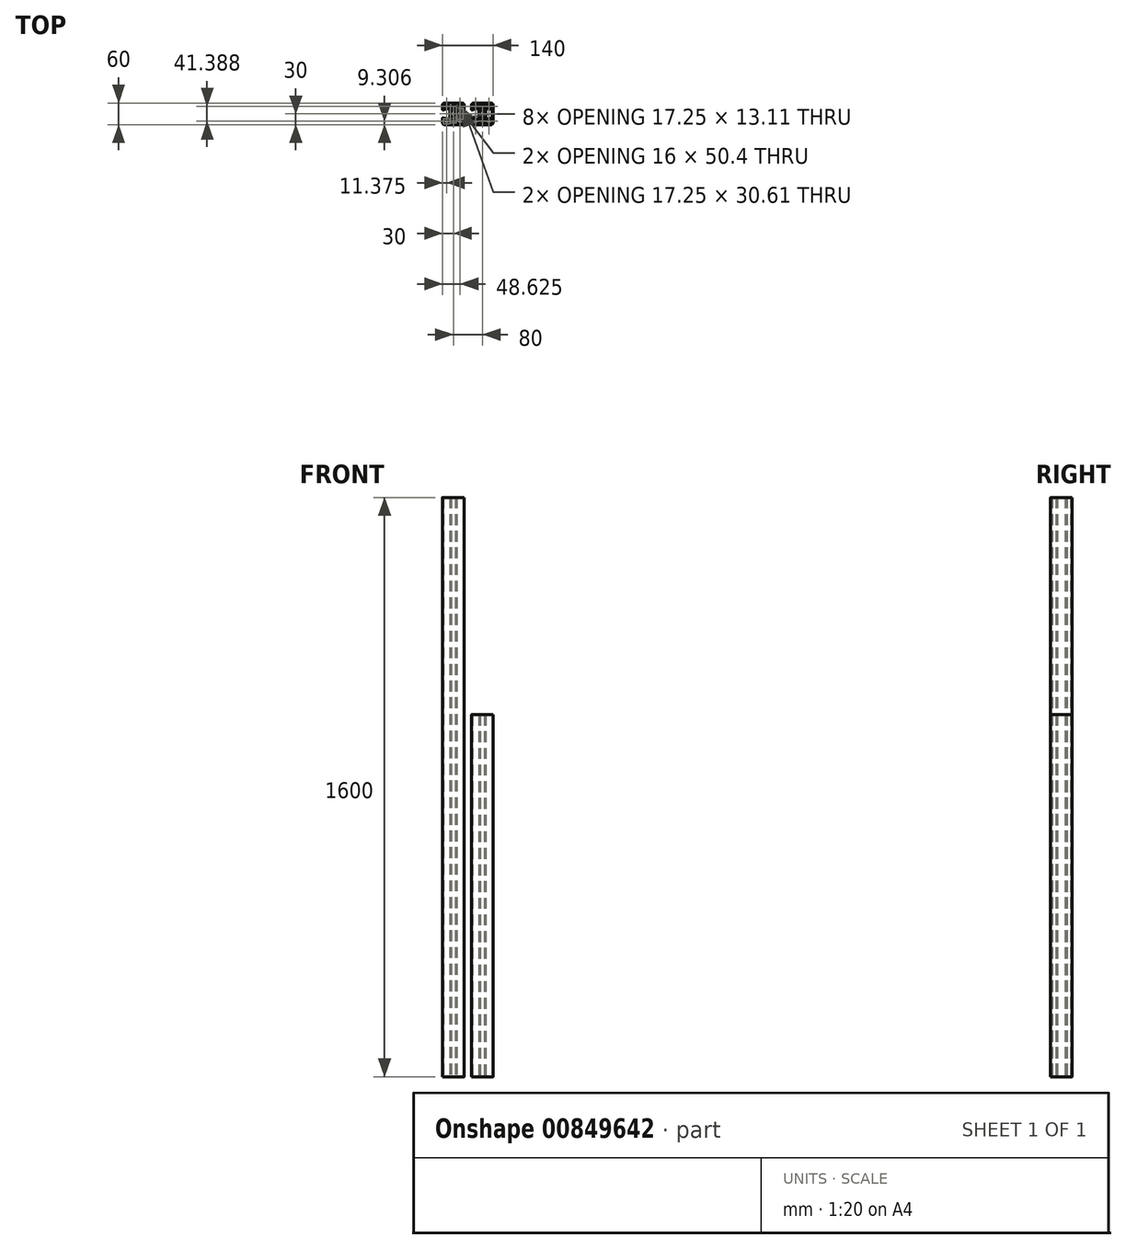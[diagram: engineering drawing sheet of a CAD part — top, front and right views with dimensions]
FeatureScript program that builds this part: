
annotation { "Feature Type Name" : "Feature", "Feature Type Description" : "" }
export const myFeature = defineFeature(function(context is Context, id is Id, definition is map)
    precondition{}
    {
        {
            var Q0;
            Q0=qCreatedBy(makeId("Top.planeOp"),FACE);
            var sketch = newSketch(context, id + "F0", { "sketchPlane" : qUnion([Q0])});
            skLineSegment(sketch, "E0", {"start": v(11.26, -15.27) * mm, "end": v(26.88, -11.09) * mm});
            skLineSegment(sketch, "E1", {"start": v(27.25, -10.6) * mm, "end": v(27.25, 10.6) * mm});
            skLineSegment(sketch, "E2", {"start": v(26.88, 11.09) * mm, "end": v(11.26, 15.27) * mm});
            skLineSegment(sketch, "E3", {"start": v(10, 14.3) * mm, "end": v(10, -14.3) * mm});
            skLineSegment(sketch, "E4", {"start": v(24, 27.25) * mm, "end": v(11, 27.25) * mm});
            skLineSegment(sketch, "E5", {"start": v(10, 26.25) * mm, "end": v(10, 19.22) * mm});
            skLineSegment(sketch, "E6", {"start": v(10.74, 18.26) * mm, "end": v(26, 14.17) * mm});
            skLineSegment(sketch, "E7", {"start": v(27.25, 15.14) * mm, "end": v(27.25, 24) * mm});
            skLineSegment(sketch, "E8", {"start": v(26, -14.17) * mm, "end": v(10.74, -18.26) * mm});
            skLineSegment(sketch, "E9", {"start": v(10, -19.22) * mm, "end": v(10, -26.25) * mm});
            skLineSegment(sketch, "E10", {"start": v(11, -27.25) * mm, "end": v(24, -27.25) * mm});
            skLineSegment(sketch, "E11", {"start": v(27.25, -24) * mm, "end": v(27.25, -15.14) * mm});
            skLineSegment(sketch, "E12", {"start": v(-10, 14.3) * mm, "end": v(-10, -14.3) * mm});
            skLineSegment(sketch, "E13", {"start": v(-28.43, 10.67) * mm, "end": v(-11.26, 15.27) * mm});
            skLineSegment(sketch, "E14", {"start": v(-30, 24) * mm, "end": v(-30, 11.88) * mm});
            skLineSegment(sketch, "E15", {"start": v(24, 30) * mm, "end": v(-24, 30) * mm});
            skLineSegment(sketch, "E16", {"start": v(30, -24) * mm, "end": v(30, 24) * mm});
            skLineSegment(sketch, "E17", {"start": v(-24, -30) * mm, "end": v(24, -30) * mm});
            skLineSegment(sketch, "E18", {"start": v(-30, -11.88) * mm, "end": v(-30, -24) * mm});
            skLineSegment(sketch, "E19", {"start": v(-11.26, -15.27) * mm, "end": v(-28.43, -10.67) * mm});
            skLineSegment(sketch, "E20", {"start": v(-26, 14.17) * mm, "end": v(-10.74, 18.26) * mm});
            skLineSegment(sketch, "E21", {"start": v(-10, 19.22) * mm, "end": v(-10, 26.25) * mm});
            skLineSegment(sketch, "E22", {"start": v(-11, 27.25) * mm, "end": v(-24, 27.25) * mm});
            skLineSegment(sketch, "E23", {"start": v(-27.25, 24) * mm, "end": v(-27.25, 15.14) * mm});
            skLineSegment(sketch, "E24", {"start": v(-24, -27.25) * mm, "end": v(-11, -27.25) * mm});
            skLineSegment(sketch, "E25", {"start": v(-10, -26.25) * mm, "end": v(-10, -19.22) * mm});
            skLineSegment(sketch, "E26", {"start": v(-10.74, -18.26) * mm, "end": v(-26, -14.17) * mm});
            skLineSegment(sketch, "E27", {"start": v(-27.25, -15.14) * mm, "end": v(-27.25, -24) * mm});
            skLineSegment(sketch, "E28", {"start": v(5.2, 25.2) * mm, "end": v(-5.2, 25.2) * mm});
            skLineSegment(sketch, "E29", {"start": v(-6.2, 24.2) * mm, "end": v(-6.2, 5.4) * mm});
            skLineSegment(sketch, "E30", {"start": v(-6.2, -5.4) * mm, "end": v(-6.2, -24.2) * mm});
            skLineSegment(sketch, "E31", {"start": v(-5.2, -25.2) * mm, "end": v(5.2, -25.2) * mm});
            skLineSegment(sketch, "E32", {"start": v(6.2, -24.2) * mm, "end": v(6.2, -5.4) * mm});
            skLineSegment(sketch, "E33", {"start": v(6.2, 5.4) * mm, "end": v(6.2, 24.2) * mm});
            skArc(sketch, "E34", {"start": v(10, -14.3) * mm, "mid": v(10.4, -15.1) * mm, "end": v(11.26, -15.27) * mm});
            skArc(sketch, "E35", {"start": v(26.88, -11.09) * mm, "mid": v(27.15, -10.9) * mm, "end": v(27.25, -10.6) * mm});
            skArc(sketch, "E36", {"start": v(27.25, 10.6) * mm, "mid": v(27.15, 10.9) * mm, "end": v(26.88, 11.09) * mm});
            skArc(sketch, "E37", {"start": v(11.26, 15.27) * mm, "mid": v(10.4, 15.1) * mm, "end": v(10, 14.3) * mm});
            skArc(sketch, "E38", {"start": v(11, 27.25) * mm, "mid": v(10.3, 26.96) * mm, "end": v(10, 26.25) * mm});
            skArc(sketch, "E39", {"start": v(10, 19.22) * mm, "mid": v(10.2, 18.61) * mm, "end": v(10.74, 18.26) * mm});
            skArc(sketch, "E40", {"start": v(26, 14.17) * mm, "mid": v(26.86, 14.34) * mm, "end": v(27.25, 15.14) * mm});
            skArc(sketch, "E41", {"start": v(27.25, 24) * mm, "mid": v(26.3, 26.3) * mm, "end": v(24, 27.25) * mm});
            skArc(sketch, "E42", {"start": v(27.25, -15.14) * mm, "mid": v(26.86, -14.34) * mm, "end": v(26, -14.17) * mm});
            skArc(sketch, "E43", {"start": v(10.74, -18.26) * mm, "mid": v(10.2, -18.61) * mm, "end": v(10, -19.22) * mm});
            skArc(sketch, "E44", {"start": v(10, -26.25) * mm, "mid": v(10.3, -26.96) * mm, "end": v(11, -27.25) * mm});
            skArc(sketch, "E45", {"start": v(24, -27.25) * mm, "mid": v(26.3, -26.3) * mm, "end": v(27.25, -24) * mm});
            skArc(sketch, "E46", {"start": v(-11.26, -15.27) * mm, "mid": v(-10.4, -15.1) * mm, "end": v(-10, -14.3) * mm});
            skArc(sketch, "E47", {"start": v(-10, 14.3) * mm, "mid": v(-10.4, 15.1) * mm, "end": v(-11.26, 15.27) * mm});
            skArc(sketch, "E48", {"start": v(-30, 11.88) * mm, "mid": v(-29.51, 10.89) * mm, "end": v(-28.43, 10.67) * mm});
            skArc(sketch, "E49", {"start": v(-24, 30) * mm, "mid": v(-28.24, 28.24) * mm, "end": v(-30, 24) * mm});
            skArc(sketch, "E50", {"start": v(30, 24) * mm, "mid": v(28.24, 28.24) * mm, "end": v(24, 30) * mm});
            skArc(sketch, "E51", {"start": v(24, -30) * mm, "mid": v(28.24, -28.24) * mm, "end": v(30, -24) * mm});
            skArc(sketch, "E52", {"start": v(-30, -24) * mm, "mid": v(-28.24, -28.24) * mm, "end": v(-24, -30) * mm});
            skArc(sketch, "E53", {"start": v(-28.43, -10.67) * mm, "mid": v(-29.51, -10.89) * mm, "end": v(-30, -11.88) * mm});
            skArc(sketch, "E54", {"start": v(-27.25, 15.14) * mm, "mid": v(-26.86, 14.34) * mm, "end": v(-26, 14.17) * mm});
            skArc(sketch, "E55", {"start": v(-10.74, 18.26) * mm, "mid": v(-10.2, 18.61) * mm, "end": v(-10, 19.22) * mm});
            skArc(sketch, "E56", {"start": v(-10, 26.25) * mm, "mid": v(-10.3, 26.96) * mm, "end": v(-11, 27.25) * mm});
            skArc(sketch, "E57", {"start": v(-24, 27.25) * mm, "mid": v(-26.3, 26.3) * mm, "end": v(-27.25, 24) * mm});
            skArc(sketch, "E58", {"start": v(-27.25, -24) * mm, "mid": v(-26.3, -26.3) * mm, "end": v(-24, -27.25) * mm});
            skArc(sketch, "E59", {"start": v(-11, -27.25) * mm, "mid": v(-10.3, -26.96) * mm, "end": v(-10, -26.25) * mm});
            skArc(sketch, "E60", {"start": v(-10, -19.22) * mm, "mid": v(-10.2, -18.61) * mm, "end": v(-10.74, -18.26) * mm});
            skArc(sketch, "E61", {"start": v(-26, -14.17) * mm, "mid": v(-26.86, -14.34) * mm, "end": v(-27.25, -15.14) * mm});
            skArc(sketch, "E62", {"start": v(6.2, 24.2) * mm, "mid": v(5.9, 24.9) * mm, "end": v(5.2, 25.2) * mm});
            skArc(sketch, "E63", {"start": v(-5.2, 25.2) * mm, "mid": v(-5.9, 24.9) * mm, "end": v(-6.2, 24.2) * mm});
            skArc(sketch, "E64", {"start": v(-6.4, 4.8) * mm, "mid": v(-6.25, 5.08) * mm, "end": v(-6.2, 5.4) * mm});
            skArc(sketch, "E65", {"start": v(-6.4, 4.8) * mm, "mid": v(-8, 0) * mm, "end": v(-6.4, -4.8) * mm});
            skArc(sketch, "E66", {"start": v(-6.2, -5.4) * mm, "mid": v(-6.25, -5.08) * mm, "end": v(-6.4, -4.8) * mm});
            skArc(sketch, "E67", {"start": v(-6.2, -24.2) * mm, "mid": v(-5.9, -24.9) * mm, "end": v(-5.2, -25.2) * mm});
            skArc(sketch, "E68", {"start": v(5.2, -25.2) * mm, "mid": v(5.9, -24.9) * mm, "end": v(6.2, -24.2) * mm});
            skArc(sketch, "E69", {"start": v(6.4, -4.8) * mm, "mid": v(6.25, -5.08) * mm, "end": v(6.2, -5.4) * mm});
            skArc(sketch, "E70", {"start": v(6.4, -4.8) * mm, "mid": v(8, 0) * mm, "end": v(6.4, 4.8) * mm});
            skArc(sketch, "E71", {"start": v(6.2, 5.4) * mm, "mid": v(6.25, 5.08) * mm, "end": v(6.4, 4.8) * mm});
            skLineSegment(sketch, "E72.1.0.0", {"start": v(52.75, -15.14) * mm, "end": v(52.75, -24) * mm});
            skLineSegment(sketch, "E72.1.0.1", {"start": v(70, -26.25) * mm, "end": v(70, -19.22) * mm});
            skArc(sketch, "E72.1.0.2", {"start": v(56, 27.25) * mm, "mid": v(53.7, 26.3) * mm, "end": v(52.75, 24) * mm});
            skArc(sketch, "E72.1.0.3", {"start": v(107.25, 24) * mm, "mid": v(106.3, 26.3) * mm, "end": v(104, 27.25) * mm});
            skLineSegment(sketch, "E72.1.0.4", {"start": v(52.75, 24) * mm, "end": v(52.75, 15.14) * mm});
            skArc(sketch, "E72.1.0.5", {"start": v(50, -24) * mm, "mid": v(51.76, -28.24) * mm, "end": v(56, -30) * mm});
            skArc(sketch, "E72.1.0.6", {"start": v(104, -27.25) * mm, "mid": v(106.3, -26.3) * mm, "end": v(107.25, -24) * mm});
            skLineSegment(sketch, "E72.1.0.7", {"start": v(73.8, 24.2) * mm, "end": v(73.8, 5.4) * mm});
            skLineSegment(sketch, "E72.1.0.8", {"start": v(54, 14.17) * mm, "end": v(69.26, 18.26) * mm});
            skArc(sketch, "E72.1.0.9", {"start": v(110, 24) * mm, "mid": v(108.24, 28.24) * mm, "end": v(104, 30) * mm});
            skLineSegment(sketch, "E72.1.0.10", {"start": v(50, -11.88) * mm, "end": v(50, -24) * mm});
            skLineSegment(sketch, "E72.1.0.11", {"start": v(86.2, -24.2) * mm, "end": v(86.2, -5.4) * mm});
            skLineSegment(sketch, "E72.1.0.12", {"start": v(110, -24) * mm, "end": v(110, 24) * mm});
            skLineSegment(sketch, "E72.1.0.13", {"start": v(104, 30) * mm, "end": v(56, 30) * mm});
            skLineSegment(sketch, "E72.1.0.14", {"start": v(51.57, 10.67) * mm, "end": v(68.74, 15.27) * mm});
            skLineSegment(sketch, "E72.1.0.15", {"start": v(50, 24) * mm, "end": v(50, 11.88) * mm});
            skLineSegment(sketch, "E72.1.0.16", {"start": v(85.2, 25.2) * mm, "end": v(74.8, 25.2) * mm});
            skLineSegment(sketch, "E72.1.0.17", {"start": v(69.26, -18.26) * mm, "end": v(54, -14.17) * mm});
            skLineSegment(sketch, "E72.1.0.18", {"start": v(91.26, -15.27) * mm, "end": v(106.88, -11.09) * mm});
            skLineSegment(sketch, "E72.1.0.19", {"start": v(107.25, -10.6) * mm, "end": v(107.25, 10.6) * mm});
            skArc(sketch, "E72.1.0.20", {"start": v(52.75, -24) * mm, "mid": v(53.7, -26.3) * mm, "end": v(56, -27.25) * mm});
            skLineSegment(sketch, "E72.1.0.21", {"start": v(56, -27.25) * mm, "end": v(69, -27.25) * mm});
            skLineSegment(sketch, "E72.1.0.22", {"start": v(106.88, 11.09) * mm, "end": v(91.26, 15.27) * mm});
            skLineSegment(sketch, "E72.1.0.23", {"start": v(90, 14.3) * mm, "end": v(90, -14.3) * mm});
            skLineSegment(sketch, "E72.1.0.24", {"start": v(69, 27.25) * mm, "end": v(56, 27.25) * mm});
            skLineSegment(sketch, "E72.1.0.25", {"start": v(104, 27.25) * mm, "end": v(91, 27.25) * mm});
            skLineSegment(sketch, "E72.1.0.26", {"start": v(90, 26.25) * mm, "end": v(90, 19.22) * mm});
            skArc(sketch, "E72.1.0.27", {"start": v(86.4, -4.8) * mm, "mid": v(88, 0) * mm, "end": v(86.4, 4.8) * mm});
            skLineSegment(sketch, "E72.1.0.28", {"start": v(73.8, -5.4) * mm, "end": v(73.8, -24.2) * mm});
            skLineSegment(sketch, "E72.1.0.29", {"start": v(70, 19.22) * mm, "end": v(70, 26.25) * mm});
            skLineSegment(sketch, "E72.1.0.30", {"start": v(90.74, 18.26) * mm, "end": v(106, 14.17) * mm});
            skLineSegment(sketch, "E72.1.0.31", {"start": v(107.25, 15.14) * mm, "end": v(107.25, 24) * mm});
            skArc(sketch, "E72.1.0.32", {"start": v(104, -30) * mm, "mid": v(108.24, -28.24) * mm, "end": v(110, -24) * mm});
            skLineSegment(sketch, "E72.1.0.33", {"start": v(74.8, -25.2) * mm, "end": v(85.2, -25.2) * mm});
            skLineSegment(sketch, "E72.1.0.34", {"start": v(68.74, -15.27) * mm, "end": v(51.57, -10.67) * mm});
            skLineSegment(sketch, "E72.1.0.35", {"start": v(106, -14.17) * mm, "end": v(90.74, -18.26) * mm});
            skLineSegment(sketch, "E72.1.0.36", {"start": v(90, -19.22) * mm, "end": v(90, -26.25) * mm});
            skArc(sketch, "E72.1.0.37", {"start": v(56, 30) * mm, "mid": v(51.76, 28.24) * mm, "end": v(50, 24) * mm});
            skLineSegment(sketch, "E72.1.0.38", {"start": v(86.2, 5.4) * mm, "end": v(86.2, 24.2) * mm});
            skLineSegment(sketch, "E72.1.0.39", {"start": v(56, -30) * mm, "end": v(104, -30) * mm});
            skLineSegment(sketch, "E72.1.0.40", {"start": v(91, -27.25) * mm, "end": v(104, -27.25) * mm});
            skArc(sketch, "E72.1.0.41", {"start": v(73.6, 4.8) * mm, "mid": v(72, 0) * mm, "end": v(73.6, -4.8) * mm});
            skLineSegment(sketch, "E72.1.0.42", {"start": v(107.25, -24) * mm, "end": v(107.25, -15.14) * mm});
            skLineSegment(sketch, "E72.1.0.43", {"start": v(70, 14.3) * mm, "end": v(70, -14.3) * mm});
            skArc(sketch, "E72.1.0.44", {"start": v(69, -27.25) * mm, "mid": v(69.7, -26.96) * mm, "end": v(70, -26.25) * mm});
            skArc(sketch, "E72.1.0.45", {"start": v(90.74, -18.26) * mm, "mid": v(90.2, -18.61) * mm, "end": v(90, -19.22) * mm});
            skArc(sketch, "E72.1.0.46", {"start": v(86.2, 5.4) * mm, "mid": v(86.25, 5.08) * mm, "end": v(86.4, 4.8) * mm});
            skArc(sketch, "E72.1.0.47", {"start": v(69.26, 18.26) * mm, "mid": v(69.8, 18.61) * mm, "end": v(70, 19.22) * mm});
            skArc(sketch, "E72.1.0.48", {"start": v(90, 19.22) * mm, "mid": v(90.2, 18.61) * mm, "end": v(90.74, 18.26) * mm});
            skArc(sketch, "E72.1.0.49", {"start": v(107.25, 10.6) * mm, "mid": v(107.15, 10.9) * mm, "end": v(106.88, 11.09) * mm});
            skArc(sketch, "E72.1.0.50", {"start": v(54, -14.17) * mm, "mid": v(53.14, -14.34) * mm, "end": v(52.75, -15.14) * mm});
            skArc(sketch, "E72.1.0.51", {"start": v(85.2, -25.2) * mm, "mid": v(85.9, -24.9) * mm, "end": v(86.2, -24.2) * mm});
            skArc(sketch, "E72.1.0.52", {"start": v(90, -14.3) * mm, "mid": v(90.4, -15.1) * mm, "end": v(91.26, -15.27) * mm});
            skArc(sketch, "E72.1.0.53", {"start": v(73.8, -5.4) * mm, "mid": v(73.75, -5.08) * mm, "end": v(73.6, -4.8) * mm});
            skArc(sketch, "E72.1.0.54", {"start": v(50, 11.88) * mm, "mid": v(50.49, 10.89) * mm, "end": v(51.57, 10.67) * mm});
            skArc(sketch, "E72.1.0.55", {"start": v(73.6, 4.8) * mm, "mid": v(73.75, 5.08) * mm, "end": v(73.8, 5.4) * mm});
            skArc(sketch, "E72.1.0.56", {"start": v(70, -19.22) * mm, "mid": v(69.8, -18.61) * mm, "end": v(69.26, -18.26) * mm});
            skArc(sketch, "E72.1.0.57", {"start": v(90, -26.25) * mm, "mid": v(90.3, -26.96) * mm, "end": v(91, -27.25) * mm});
            skArc(sketch, "E72.1.0.58", {"start": v(107.25, -15.14) * mm, "mid": v(106.86, -14.34) * mm, "end": v(106, -14.17) * mm});
            skArc(sketch, "E72.1.0.59", {"start": v(70, 26.25) * mm, "mid": v(69.7, 26.96) * mm, "end": v(69, 27.25) * mm});
            skArc(sketch, "E72.1.0.60", {"start": v(106, 14.17) * mm, "mid": v(106.86, 14.34) * mm, "end": v(107.25, 15.14) * mm});
            skArc(sketch, "E72.1.0.61", {"start": v(52.75, 15.14) * mm, "mid": v(53.14, 14.34) * mm, "end": v(54, 14.17) * mm});
            skArc(sketch, "E72.1.0.62", {"start": v(91, 27.25) * mm, "mid": v(90.3, 26.96) * mm, "end": v(90, 26.25) * mm});
            skArc(sketch, "E72.1.0.63", {"start": v(68.74, -15.27) * mm, "mid": v(69.6, -15.1) * mm, "end": v(70, -14.3) * mm});
            skArc(sketch, "E72.1.0.64", {"start": v(51.57, -10.67) * mm, "mid": v(50.49, -10.89) * mm, "end": v(50, -11.88) * mm});
            skArc(sketch, "E72.1.0.65", {"start": v(91.26, 15.27) * mm, "mid": v(90.4, 15.1) * mm, "end": v(90, 14.3) * mm});
            skArc(sketch, "E72.1.0.66", {"start": v(86.4, -4.8) * mm, "mid": v(86.25, -5.08) * mm, "end": v(86.2, -5.4) * mm});
            skArc(sketch, "E72.1.0.67", {"start": v(86.2, 24.2) * mm, "mid": v(85.9, 24.9) * mm, "end": v(85.2, 25.2) * mm});
            skArc(sketch, "E72.1.0.68", {"start": v(70, 14.3) * mm, "mid": v(69.6, 15.1) * mm, "end": v(68.74, 15.27) * mm});
            skArc(sketch, "E72.1.0.69", {"start": v(106.88, -11.09) * mm, "mid": v(107.15, -10.9) * mm, "end": v(107.25, -10.6) * mm});
            skArc(sketch, "E72.1.0.70", {"start": v(74.8, 25.2) * mm, "mid": v(74.1, 24.9) * mm, "end": v(73.8, 24.2) * mm});
            skArc(sketch, "E72.1.0.71", {"start": v(73.8, -24.2) * mm, "mid": v(74.1, -24.9) * mm, "end": v(74.8, -25.2) * mm});
            skLineSegment(sketch, "E72.2.0.0", {"start": v(132.75, -15.14) * mm, "end": v(132.75, -24) * mm});
            skLineSegment(sketch, "E72.2.0.1", {"start": v(150, -26.25) * mm, "end": v(150, -19.22) * mm});
            skArc(sketch, "E72.2.0.2", {"start": v(136, 27.25) * mm, "mid": v(133.7, 26.3) * mm, "end": v(132.75, 24) * mm});
            skArc(sketch, "E72.2.0.3", {"start": v(187.25, 24) * mm, "mid": v(186.3, 26.3) * mm, "end": v(184, 27.25) * mm});
            skLineSegment(sketch, "E72.2.0.4", {"start": v(132.75, 24) * mm, "end": v(132.75, 15.14) * mm});
            skArc(sketch, "E72.2.0.5", {"start": v(130, -24) * mm, "mid": v(131.76, -28.24) * mm, "end": v(136, -30) * mm});
            skArc(sketch, "E72.2.0.6", {"start": v(184, -27.25) * mm, "mid": v(186.3, -26.3) * mm, "end": v(187.25, -24) * mm});
            skLineSegment(sketch, "E72.2.0.7", {"start": v(153.8, 24.2) * mm, "end": v(153.8, 5.4) * mm});
            skLineSegment(sketch, "E72.2.0.8", {"start": v(134, 14.17) * mm, "end": v(149.26, 18.26) * mm});
            skArc(sketch, "E72.2.0.9", {"start": v(190, 24) * mm, "mid": v(188.24, 28.24) * mm, "end": v(184, 30) * mm});
            skLineSegment(sketch, "E72.2.0.10", {"start": v(130, -11.88) * mm, "end": v(130, -24) * mm});
            skLineSegment(sketch, "E72.2.0.11", {"start": v(166.2, -24.2) * mm, "end": v(166.2, -5.4) * mm});
            skLineSegment(sketch, "E72.2.0.12", {"start": v(190, -24) * mm, "end": v(190, 24) * mm});
            skLineSegment(sketch, "E72.2.0.13", {"start": v(184, 30) * mm, "end": v(136, 30) * mm});
            skLineSegment(sketch, "E72.2.0.14", {"start": v(131.57, 10.67) * mm, "end": v(148.74, 15.27) * mm});
            skLineSegment(sketch, "E72.2.0.15", {"start": v(130, 24) * mm, "end": v(130, 11.88) * mm});
            skLineSegment(sketch, "E72.2.0.16", {"start": v(165.2, 25.2) * mm, "end": v(154.8, 25.2) * mm});
            skLineSegment(sketch, "E72.2.0.17", {"start": v(149.26, -18.26) * mm, "end": v(134, -14.17) * mm});
            skLineSegment(sketch, "E72.2.0.18", {"start": v(171.26, -15.27) * mm, "end": v(186.88, -11.09) * mm});
            skLineSegment(sketch, "E72.2.0.19", {"start": v(187.25, -10.6) * mm, "end": v(187.25, 10.6) * mm});
            skArc(sketch, "E72.2.0.20", {"start": v(132.75, -24) * mm, "mid": v(133.7, -26.3) * mm, "end": v(136, -27.25) * mm});
            skLineSegment(sketch, "E72.2.0.21", {"start": v(136, -27.25) * mm, "end": v(149, -27.25) * mm});
            skLineSegment(sketch, "E72.2.0.22", {"start": v(186.88, 11.09) * mm, "end": v(171.26, 15.27) * mm});
            skLineSegment(sketch, "E72.2.0.23", {"start": v(170, 14.3) * mm, "end": v(170, -14.3) * mm});
            skLineSegment(sketch, "E72.2.0.24", {"start": v(149, 27.25) * mm, "end": v(136, 27.25) * mm});
            skLineSegment(sketch, "E72.2.0.25", {"start": v(184, 27.25) * mm, "end": v(171, 27.25) * mm});
            skLineSegment(sketch, "E72.2.0.26", {"start": v(170, 26.25) * mm, "end": v(170, 19.22) * mm});
            skArc(sketch, "E72.2.0.27", {"start": v(166.4, -4.8) * mm, "mid": v(168, 0) * mm, "end": v(166.4, 4.8) * mm});
            skLineSegment(sketch, "E72.2.0.28", {"start": v(153.8, -5.4) * mm, "end": v(153.8, -24.2) * mm});
            skLineSegment(sketch, "E72.2.0.29", {"start": v(150, 19.22) * mm, "end": v(150, 26.25) * mm});
            skLineSegment(sketch, "E72.2.0.30", {"start": v(170.74, 18.26) * mm, "end": v(186, 14.17) * mm});
            skLineSegment(sketch, "E72.2.0.31", {"start": v(187.25, 15.14) * mm, "end": v(187.25, 24) * mm});
            skArc(sketch, "E72.2.0.32", {"start": v(184, -30) * mm, "mid": v(188.24, -28.24) * mm, "end": v(190, -24) * mm});
            skLineSegment(sketch, "E72.2.0.33", {"start": v(154.8, -25.2) * mm, "end": v(165.2, -25.2) * mm});
            skLineSegment(sketch, "E72.2.0.34", {"start": v(148.74, -15.27) * mm, "end": v(131.57, -10.67) * mm});
            skLineSegment(sketch, "E72.2.0.35", {"start": v(186, -14.17) * mm, "end": v(170.74, -18.26) * mm});
            skLineSegment(sketch, "E72.2.0.36", {"start": v(170, -19.22) * mm, "end": v(170, -26.25) * mm});
            skArc(sketch, "E72.2.0.37", {"start": v(136, 30) * mm, "mid": v(131.76, 28.24) * mm, "end": v(130, 24) * mm});
            skLineSegment(sketch, "E72.2.0.38", {"start": v(166.2, 5.4) * mm, "end": v(166.2, 24.2) * mm});
            skLineSegment(sketch, "E72.2.0.39", {"start": v(136, -30) * mm, "end": v(184, -30) * mm});
            skLineSegment(sketch, "E72.2.0.40", {"start": v(171, -27.25) * mm, "end": v(184, -27.25) * mm});
            skArc(sketch, "E72.2.0.41", {"start": v(153.6, 4.8) * mm, "mid": v(152, 0) * mm, "end": v(153.6, -4.8) * mm});
            skLineSegment(sketch, "E72.2.0.42", {"start": v(187.25, -24) * mm, "end": v(187.25, -15.14) * mm});
            skLineSegment(sketch, "E72.2.0.43", {"start": v(150, 14.3) * mm, "end": v(150, -14.3) * mm});
            skArc(sketch, "E72.2.0.44", {"start": v(149, -27.25) * mm, "mid": v(149.7, -26.96) * mm, "end": v(150, -26.25) * mm});
            skArc(sketch, "E72.2.0.45", {"start": v(170.74, -18.26) * mm, "mid": v(170.2, -18.61) * mm, "end": v(170, -19.22) * mm});
            skArc(sketch, "E72.2.0.46", {"start": v(166.2, 5.4) * mm, "mid": v(166.25, 5.08) * mm, "end": v(166.4, 4.8) * mm});
            skArc(sketch, "E72.2.0.47", {"start": v(149.26, 18.26) * mm, "mid": v(149.8, 18.61) * mm, "end": v(150, 19.22) * mm});
            skArc(sketch, "E72.2.0.48", {"start": v(170, 19.22) * mm, "mid": v(170.2, 18.61) * mm, "end": v(170.74, 18.26) * mm});
            skArc(sketch, "E72.2.0.49", {"start": v(187.25, 10.6) * mm, "mid": v(187.15, 10.9) * mm, "end": v(186.88, 11.09) * mm});
            skArc(sketch, "E72.2.0.50", {"start": v(134, -14.17) * mm, "mid": v(133.14, -14.34) * mm, "end": v(132.75, -15.14) * mm});
            skArc(sketch, "E72.2.0.51", {"start": v(165.2, -25.2) * mm, "mid": v(165.9, -24.9) * mm, "end": v(166.2, -24.2) * mm});
            skArc(sketch, "E72.2.0.52", {"start": v(170, -14.3) * mm, "mid": v(170.4, -15.1) * mm, "end": v(171.26, -15.27) * mm});
            skArc(sketch, "E72.2.0.53", {"start": v(153.8, -5.4) * mm, "mid": v(153.75, -5.08) * mm, "end": v(153.6, -4.8) * mm});
            skArc(sketch, "E72.2.0.54", {"start": v(130, 11.88) * mm, "mid": v(130.49, 10.89) * mm, "end": v(131.57, 10.67) * mm});
            skArc(sketch, "E72.2.0.55", {"start": v(153.6, 4.8) * mm, "mid": v(153.75, 5.08) * mm, "end": v(153.8, 5.4) * mm});
            skArc(sketch, "E72.2.0.56", {"start": v(150, -19.22) * mm, "mid": v(149.8, -18.61) * mm, "end": v(149.26, -18.26) * mm});
            skArc(sketch, "E72.2.0.57", {"start": v(170, -26.25) * mm, "mid": v(170.3, -26.96) * mm, "end": v(171, -27.25) * mm});
            skArc(sketch, "E72.2.0.58", {"start": v(187.25, -15.14) * mm, "mid": v(186.86, -14.34) * mm, "end": v(186, -14.17) * mm});
            skArc(sketch, "E72.2.0.59", {"start": v(150, 26.25) * mm, "mid": v(149.7, 26.96) * mm, "end": v(149, 27.25) * mm});
            skArc(sketch, "E72.2.0.60", {"start": v(186, 14.17) * mm, "mid": v(186.86, 14.34) * mm, "end": v(187.25, 15.14) * mm});
            skArc(sketch, "E72.2.0.61", {"start": v(132.75, 15.14) * mm, "mid": v(133.14, 14.34) * mm, "end": v(134, 14.17) * mm});
            skArc(sketch, "E72.2.0.62", {"start": v(171, 27.25) * mm, "mid": v(170.3, 26.96) * mm, "end": v(170, 26.25) * mm});
            skArc(sketch, "E72.2.0.63", {"start": v(148.74, -15.27) * mm, "mid": v(149.6, -15.1) * mm, "end": v(150, -14.3) * mm});
            skArc(sketch, "E72.2.0.64", {"start": v(131.57, -10.67) * mm, "mid": v(130.49, -10.89) * mm, "end": v(130, -11.88) * mm});
            skArc(sketch, "E72.2.0.65", {"start": v(171.26, 15.27) * mm, "mid": v(170.4, 15.1) * mm, "end": v(170, 14.3) * mm});
            skArc(sketch, "E72.2.0.66", {"start": v(166.4, -4.8) * mm, "mid": v(166.25, -5.08) * mm, "end": v(166.2, -5.4) * mm});
            skArc(sketch, "E72.2.0.67", {"start": v(166.2, 24.2) * mm, "mid": v(165.9, 24.9) * mm, "end": v(165.2, 25.2) * mm});
            skArc(sketch, "E72.2.0.68", {"start": v(150, 14.3) * mm, "mid": v(149.6, 15.1) * mm, "end": v(148.74, 15.27) * mm});
            skArc(sketch, "E72.2.0.69", {"start": v(186.88, -11.09) * mm, "mid": v(187.15, -10.9) * mm, "end": v(187.25, -10.6) * mm});
            skArc(sketch, "E72.2.0.70", {"start": v(154.8, 25.2) * mm, "mid": v(154.1, 24.9) * mm, "end": v(153.8, 24.2) * mm});
            skArc(sketch, "E72.2.0.71", {"start": v(153.8, -24.2) * mm, "mid": v(154.1, -24.9) * mm, "end": v(154.8, -25.2) * mm});
            skLineSegment(sketch, "E72.3.0.0", {"start": v(212.75, -15.14) * mm, "end": v(212.75, -24) * mm});
            skLineSegment(sketch, "E72.3.0.1", {"start": v(230, -26.25) * mm, "end": v(230, -19.22) * mm});
            skArc(sketch, "E72.3.0.2", {"start": v(216, 27.25) * mm, "mid": v(213.7, 26.3) * mm, "end": v(212.75, 24) * mm});
            skArc(sketch, "E72.3.0.3", {"start": v(267.25, 24) * mm, "mid": v(266.3, 26.3) * mm, "end": v(264, 27.25) * mm});
            skLineSegment(sketch, "E72.3.0.4", {"start": v(212.75, 24) * mm, "end": v(212.75, 15.14) * mm});
            skArc(sketch, "E72.3.0.5", {"start": v(210, -24) * mm, "mid": v(211.76, -28.24) * mm, "end": v(216, -30) * mm});
            skArc(sketch, "E72.3.0.6", {"start": v(264, -27.25) * mm, "mid": v(266.3, -26.3) * mm, "end": v(267.25, -24) * mm});
            skLineSegment(sketch, "E72.3.0.7", {"start": v(233.8, 24.2) * mm, "end": v(233.8, 5.4) * mm});
            skLineSegment(sketch, "E72.3.0.8", {"start": v(214, 14.17) * mm, "end": v(229.26, 18.26) * mm});
            skArc(sketch, "E72.3.0.9", {"start": v(270, 24) * mm, "mid": v(268.24, 28.24) * mm, "end": v(264, 30) * mm});
            skLineSegment(sketch, "E72.3.0.10", {"start": v(210, -11.88) * mm, "end": v(210, -24) * mm});
            skLineSegment(sketch, "E72.3.0.11", {"start": v(246.2, -24.2) * mm, "end": v(246.2, -5.4) * mm});
            skLineSegment(sketch, "E72.3.0.12", {"start": v(270, -24) * mm, "end": v(270, 24) * mm});
            skLineSegment(sketch, "E72.3.0.13", {"start": v(264, 30) * mm, "end": v(216, 30) * mm});
            skLineSegment(sketch, "E72.3.0.14", {"start": v(211.57, 10.67) * mm, "end": v(228.74, 15.27) * mm});
            skLineSegment(sketch, "E72.3.0.15", {"start": v(210, 24) * mm, "end": v(210, 11.88) * mm});
            skLineSegment(sketch, "E72.3.0.16", {"start": v(245.2, 25.2) * mm, "end": v(234.8, 25.2) * mm});
            skLineSegment(sketch, "E72.3.0.17", {"start": v(229.26, -18.26) * mm, "end": v(214, -14.17) * mm});
            skLineSegment(sketch, "E72.3.0.18", {"start": v(251.26, -15.27) * mm, "end": v(266.88, -11.09) * mm});
            skLineSegment(sketch, "E72.3.0.19", {"start": v(267.25, -10.6) * mm, "end": v(267.25, 10.6) * mm});
            skArc(sketch, "E72.3.0.20", {"start": v(212.75, -24) * mm, "mid": v(213.7, -26.3) * mm, "end": v(216, -27.25) * mm});
            skLineSegment(sketch, "E72.3.0.21", {"start": v(216, -27.25) * mm, "end": v(229, -27.25) * mm});
            skLineSegment(sketch, "E72.3.0.22", {"start": v(266.88, 11.09) * mm, "end": v(251.26, 15.27) * mm});
            skLineSegment(sketch, "E72.3.0.23", {"start": v(250, 14.3) * mm, "end": v(250, -14.3) * mm});
            skLineSegment(sketch, "E72.3.0.24", {"start": v(229, 27.25) * mm, "end": v(216, 27.25) * mm});
            skLineSegment(sketch, "E72.3.0.25", {"start": v(264, 27.25) * mm, "end": v(251, 27.25) * mm});
            skLineSegment(sketch, "E72.3.0.26", {"start": v(250, 26.25) * mm, "end": v(250, 19.22) * mm});
            skArc(sketch, "E72.3.0.27", {"start": v(246.4, -4.8) * mm, "mid": v(248, 0) * mm, "end": v(246.4, 4.8) * mm});
            skLineSegment(sketch, "E72.3.0.28", {"start": v(233.8, -5.4) * mm, "end": v(233.8, -24.2) * mm});
            skLineSegment(sketch, "E72.3.0.29", {"start": v(230, 19.22) * mm, "end": v(230, 26.25) * mm});
            skLineSegment(sketch, "E72.3.0.30", {"start": v(250.74, 18.26) * mm, "end": v(266, 14.17) * mm});
            skLineSegment(sketch, "E72.3.0.31", {"start": v(267.25, 15.14) * mm, "end": v(267.25, 24) * mm});
            skArc(sketch, "E72.3.0.32", {"start": v(264, -30) * mm, "mid": v(268.24, -28.24) * mm, "end": v(270, -24) * mm});
            skLineSegment(sketch, "E72.3.0.33", {"start": v(234.8, -25.2) * mm, "end": v(245.2, -25.2) * mm});
            skLineSegment(sketch, "E72.3.0.34", {"start": v(228.74, -15.27) * mm, "end": v(211.57, -10.67) * mm});
            skLineSegment(sketch, "E72.3.0.35", {"start": v(266, -14.17) * mm, "end": v(250.74, -18.26) * mm});
            skLineSegment(sketch, "E72.3.0.36", {"start": v(250, -19.22) * mm, "end": v(250, -26.25) * mm});
            skArc(sketch, "E72.3.0.37", {"start": v(216, 30) * mm, "mid": v(211.76, 28.24) * mm, "end": v(210, 24) * mm});
            skLineSegment(sketch, "E72.3.0.38", {"start": v(246.2, 5.4) * mm, "end": v(246.2, 24.2) * mm});
            skLineSegment(sketch, "E72.3.0.39", {"start": v(216, -30) * mm, "end": v(264, -30) * mm});
            skLineSegment(sketch, "E72.3.0.40", {"start": v(251, -27.25) * mm, "end": v(264, -27.25) * mm});
            skArc(sketch, "E72.3.0.41", {"start": v(233.6, 4.8) * mm, "mid": v(232, 0) * mm, "end": v(233.6, -4.8) * mm});
            skLineSegment(sketch, "E72.3.0.42", {"start": v(267.25, -24) * mm, "end": v(267.25, -15.14) * mm});
            skLineSegment(sketch, "E72.3.0.43", {"start": v(230, 14.3) * mm, "end": v(230, -14.3) * mm});
            skArc(sketch, "E72.3.0.44", {"start": v(229, -27.25) * mm, "mid": v(229.7, -26.96) * mm, "end": v(230, -26.25) * mm});
            skArc(sketch, "E72.3.0.45", {"start": v(250.74, -18.26) * mm, "mid": v(250.2, -18.61) * mm, "end": v(250, -19.22) * mm});
            skArc(sketch, "E72.3.0.46", {"start": v(246.2, 5.4) * mm, "mid": v(246.25, 5.08) * mm, "end": v(246.4, 4.8) * mm});
            skArc(sketch, "E72.3.0.47", {"start": v(229.26, 18.26) * mm, "mid": v(229.8, 18.61) * mm, "end": v(230, 19.22) * mm});
            skArc(sketch, "E72.3.0.48", {"start": v(250, 19.22) * mm, "mid": v(250.2, 18.61) * mm, "end": v(250.74, 18.26) * mm});
            skArc(sketch, "E72.3.0.49", {"start": v(267.25, 10.6) * mm, "mid": v(267.15, 10.9) * mm, "end": v(266.88, 11.09) * mm});
            skArc(sketch, "E72.3.0.50", {"start": v(214, -14.17) * mm, "mid": v(213.14, -14.34) * mm, "end": v(212.75, -15.14) * mm});
            skArc(sketch, "E72.3.0.51", {"start": v(245.2, -25.2) * mm, "mid": v(245.9, -24.9) * mm, "end": v(246.2, -24.2) * mm});
            skArc(sketch, "E72.3.0.52", {"start": v(250, -14.3) * mm, "mid": v(250.4, -15.1) * mm, "end": v(251.26, -15.27) * mm});
            skArc(sketch, "E72.3.0.53", {"start": v(233.8, -5.4) * mm, "mid": v(233.75, -5.08) * mm, "end": v(233.6, -4.8) * mm});
            skArc(sketch, "E72.3.0.54", {"start": v(210, 11.88) * mm, "mid": v(210.49, 10.89) * mm, "end": v(211.57, 10.67) * mm});
            skArc(sketch, "E72.3.0.55", {"start": v(233.6, 4.8) * mm, "mid": v(233.75, 5.08) * mm, "end": v(233.8, 5.4) * mm});
            skArc(sketch, "E72.3.0.56", {"start": v(230, -19.22) * mm, "mid": v(229.8, -18.61) * mm, "end": v(229.26, -18.26) * mm});
            skArc(sketch, "E72.3.0.57", {"start": v(250, -26.25) * mm, "mid": v(250.3, -26.96) * mm, "end": v(251, -27.25) * mm});
            skArc(sketch, "E72.3.0.58", {"start": v(267.25, -15.14) * mm, "mid": v(266.86, -14.34) * mm, "end": v(266, -14.17) * mm});
            skArc(sketch, "E72.3.0.59", {"start": v(230, 26.25) * mm, "mid": v(229.7, 26.96) * mm, "end": v(229, 27.25) * mm});
            skArc(sketch, "E72.3.0.60", {"start": v(266, 14.17) * mm, "mid": v(266.86, 14.34) * mm, "end": v(267.25, 15.14) * mm});
            skArc(sketch, "E72.3.0.61", {"start": v(212.75, 15.14) * mm, "mid": v(213.14, 14.34) * mm, "end": v(214, 14.17) * mm});
            skArc(sketch, "E72.3.0.62", {"start": v(251, 27.25) * mm, "mid": v(250.3, 26.96) * mm, "end": v(250, 26.25) * mm});
            skArc(sketch, "E72.3.0.63", {"start": v(228.74, -15.27) * mm, "mid": v(229.6, -15.1) * mm, "end": v(230, -14.3) * mm});
            skArc(sketch, "E72.3.0.64", {"start": v(211.57, -10.67) * mm, "mid": v(210.49, -10.89) * mm, "end": v(210, -11.88) * mm});
            skArc(sketch, "E72.3.0.65", {"start": v(251.26, 15.27) * mm, "mid": v(250.4, 15.1) * mm, "end": v(250, 14.3) * mm});
            skArc(sketch, "E72.3.0.66", {"start": v(246.4, -4.8) * mm, "mid": v(246.25, -5.08) * mm, "end": v(246.2, -5.4) * mm});
            skArc(sketch, "E72.3.0.67", {"start": v(246.2, 24.2) * mm, "mid": v(245.9, 24.9) * mm, "end": v(245.2, 25.2) * mm});
            skArc(sketch, "E72.3.0.68", {"start": v(230, 14.3) * mm, "mid": v(229.6, 15.1) * mm, "end": v(228.74, 15.27) * mm});
            skArc(sketch, "E72.3.0.69", {"start": v(266.88, -11.09) * mm, "mid": v(267.15, -10.9) * mm, "end": v(267.25, -10.6) * mm});
            skArc(sketch, "E72.3.0.70", {"start": v(234.8, 25.2) * mm, "mid": v(234.1, 24.9) * mm, "end": v(233.8, 24.2) * mm});
            skArc(sketch, "E72.3.0.71", {"start": v(233.8, -24.2) * mm, "mid": v(234.1, -24.9) * mm, "end": v(234.8, -25.2) * mm});
            skLineSegment(sketch, "E72.4.0.0", {"start": v(292.75, -15.14) * mm, "end": v(292.75, -24) * mm});
            skLineSegment(sketch, "E72.4.0.1", {"start": v(310, -26.25) * mm, "end": v(310, -19.22) * mm});
            skArc(sketch, "E72.4.0.2", {"start": v(296, 27.25) * mm, "mid": v(293.7, 26.3) * mm, "end": v(292.75, 24) * mm});
            skArc(sketch, "E72.4.0.3", {"start": v(347.25, 24) * mm, "mid": v(346.3, 26.3) * mm, "end": v(344, 27.25) * mm});
            skLineSegment(sketch, "E72.4.0.4", {"start": v(292.75, 24) * mm, "end": v(292.75, 15.14) * mm});
            skArc(sketch, "E72.4.0.5", {"start": v(290, -24) * mm, "mid": v(291.76, -28.24) * mm, "end": v(296, -30) * mm});
            skArc(sketch, "E72.4.0.6", {"start": v(344, -27.25) * mm, "mid": v(346.3, -26.3) * mm, "end": v(347.25, -24) * mm});
            skLineSegment(sketch, "E72.4.0.7", {"start": v(313.8, 24.2) * mm, "end": v(313.8, 5.4) * mm});
            skLineSegment(sketch, "E72.4.0.8", {"start": v(294, 14.17) * mm, "end": v(309.26, 18.26) * mm});
            skArc(sketch, "E72.4.0.9", {"start": v(350, 24) * mm, "mid": v(348.24, 28.24) * mm, "end": v(344, 30) * mm});
            skLineSegment(sketch, "E72.4.0.10", {"start": v(290, -11.88) * mm, "end": v(290, -24) * mm});
            skLineSegment(sketch, "E72.4.0.11", {"start": v(326.2, -24.2) * mm, "end": v(326.2, -5.4) * mm});
            skLineSegment(sketch, "E72.4.0.12", {"start": v(350, -24) * mm, "end": v(350, 24) * mm});
            skLineSegment(sketch, "E72.4.0.13", {"start": v(344, 30) * mm, "end": v(296, 30) * mm});
            skLineSegment(sketch, "E72.4.0.14", {"start": v(291.57, 10.67) * mm, "end": v(308.74, 15.27) * mm});
            skLineSegment(sketch, "E72.4.0.15", {"start": v(290, 24) * mm, "end": v(290, 11.88) * mm});
            skLineSegment(sketch, "E72.4.0.16", {"start": v(325.2, 25.2) * mm, "end": v(314.8, 25.2) * mm});
            skLineSegment(sketch, "E72.4.0.17", {"start": v(309.26, -18.26) * mm, "end": v(294, -14.17) * mm});
            skLineSegment(sketch, "E72.4.0.18", {"start": v(331.26, -15.27) * mm, "end": v(346.88, -11.09) * mm});
            skLineSegment(sketch, "E72.4.0.19", {"start": v(347.25, -10.6) * mm, "end": v(347.25, 10.6) * mm});
            skArc(sketch, "E72.4.0.20", {"start": v(292.75, -24) * mm, "mid": v(293.7, -26.3) * mm, "end": v(296, -27.25) * mm});
            skLineSegment(sketch, "E72.4.0.21", {"start": v(296, -27.25) * mm, "end": v(309, -27.25) * mm});
            skLineSegment(sketch, "E72.4.0.22", {"start": v(346.88, 11.09) * mm, "end": v(331.26, 15.27) * mm});
            skLineSegment(sketch, "E72.4.0.23", {"start": v(330, 14.3) * mm, "end": v(330, -14.3) * mm});
            skLineSegment(sketch, "E72.4.0.24", {"start": v(309, 27.25) * mm, "end": v(296, 27.25) * mm});
            skLineSegment(sketch, "E72.4.0.25", {"start": v(344, 27.25) * mm, "end": v(331, 27.25) * mm});
            skLineSegment(sketch, "E72.4.0.26", {"start": v(330, 26.25) * mm, "end": v(330, 19.22) * mm});
            skArc(sketch, "E72.4.0.27", {"start": v(326.4, -4.8) * mm, "mid": v(328, 0) * mm, "end": v(326.4, 4.8) * mm});
            skLineSegment(sketch, "E72.4.0.28", {"start": v(313.8, -5.4) * mm, "end": v(313.8, -24.2) * mm});
            skLineSegment(sketch, "E72.4.0.29", {"start": v(310, 19.22) * mm, "end": v(310, 26.25) * mm});
            skLineSegment(sketch, "E72.4.0.30", {"start": v(330.74, 18.26) * mm, "end": v(346, 14.17) * mm});
            skLineSegment(sketch, "E72.4.0.31", {"start": v(347.25, 15.14) * mm, "end": v(347.25, 24) * mm});
            skArc(sketch, "E72.4.0.32", {"start": v(344, -30) * mm, "mid": v(348.24, -28.24) * mm, "end": v(350, -24) * mm});
            skLineSegment(sketch, "E72.4.0.33", {"start": v(314.8, -25.2) * mm, "end": v(325.2, -25.2) * mm});
            skLineSegment(sketch, "E72.4.0.34", {"start": v(308.74, -15.27) * mm, "end": v(291.57, -10.67) * mm});
            skLineSegment(sketch, "E72.4.0.35", {"start": v(346, -14.17) * mm, "end": v(330.74, -18.26) * mm});
            skLineSegment(sketch, "E72.4.0.36", {"start": v(330, -19.22) * mm, "end": v(330, -26.25) * mm});
            skArc(sketch, "E72.4.0.37", {"start": v(296, 30) * mm, "mid": v(291.76, 28.24) * mm, "end": v(290, 24) * mm});
            skLineSegment(sketch, "E72.4.0.38", {"start": v(326.2, 5.4) * mm, "end": v(326.2, 24.2) * mm});
            skLineSegment(sketch, "E72.4.0.39", {"start": v(296, -30) * mm, "end": v(344, -30) * mm});
            skLineSegment(sketch, "E72.4.0.40", {"start": v(331, -27.25) * mm, "end": v(344, -27.25) * mm});
            skArc(sketch, "E72.4.0.41", {"start": v(313.6, 4.8) * mm, "mid": v(312, 0) * mm, "end": v(313.6, -4.8) * mm});
            skLineSegment(sketch, "E72.4.0.42", {"start": v(347.25, -24) * mm, "end": v(347.25, -15.14) * mm});
            skLineSegment(sketch, "E72.4.0.43", {"start": v(310, 14.3) * mm, "end": v(310, -14.3) * mm});
            skArc(sketch, "E72.4.0.44", {"start": v(309, -27.25) * mm, "mid": v(309.7, -26.96) * mm, "end": v(310, -26.25) * mm});
            skArc(sketch, "E72.4.0.45", {"start": v(330.74, -18.26) * mm, "mid": v(330.2, -18.61) * mm, "end": v(330, -19.22) * mm});
            skArc(sketch, "E72.4.0.46", {"start": v(326.2, 5.4) * mm, "mid": v(326.25, 5.08) * mm, "end": v(326.4, 4.8) * mm});
            skArc(sketch, "E72.4.0.47", {"start": v(309.26, 18.26) * mm, "mid": v(309.8, 18.61) * mm, "end": v(310, 19.22) * mm});
            skArc(sketch, "E72.4.0.48", {"start": v(330, 19.22) * mm, "mid": v(330.2, 18.61) * mm, "end": v(330.74, 18.26) * mm});
            skArc(sketch, "E72.4.0.49", {"start": v(347.25, 10.6) * mm, "mid": v(347.15, 10.9) * mm, "end": v(346.88, 11.09) * mm});
            skArc(sketch, "E72.4.0.50", {"start": v(294, -14.17) * mm, "mid": v(293.14, -14.34) * mm, "end": v(292.75, -15.14) * mm});
            skArc(sketch, "E72.4.0.51", {"start": v(325.2, -25.2) * mm, "mid": v(325.9, -24.9) * mm, "end": v(326.2, -24.2) * mm});
            skArc(sketch, "E72.4.0.52", {"start": v(330, -14.3) * mm, "mid": v(330.4, -15.1) * mm, "end": v(331.26, -15.27) * mm});
            skArc(sketch, "E72.4.0.53", {"start": v(313.8, -5.4) * mm, "mid": v(313.75, -5.08) * mm, "end": v(313.6, -4.8) * mm});
            skArc(sketch, "E72.4.0.54", {"start": v(290, 11.88) * mm, "mid": v(290.49, 10.89) * mm, "end": v(291.57, 10.67) * mm});
            skArc(sketch, "E72.4.0.55", {"start": v(313.6, 4.8) * mm, "mid": v(313.75, 5.08) * mm, "end": v(313.8, 5.4) * mm});
            skArc(sketch, "E72.4.0.56", {"start": v(310, -19.22) * mm, "mid": v(309.8, -18.61) * mm, "end": v(309.26, -18.26) * mm});
            skArc(sketch, "E72.4.0.57", {"start": v(330, -26.25) * mm, "mid": v(330.3, -26.96) * mm, "end": v(331, -27.25) * mm});
            skArc(sketch, "E72.4.0.58", {"start": v(347.25, -15.14) * mm, "mid": v(346.86, -14.34) * mm, "end": v(346, -14.17) * mm});
            skArc(sketch, "E72.4.0.59", {"start": v(310, 26.25) * mm, "mid": v(309.7, 26.96) * mm, "end": v(309, 27.25) * mm});
            skArc(sketch, "E72.4.0.60", {"start": v(346, 14.17) * mm, "mid": v(346.86, 14.34) * mm, "end": v(347.25, 15.14) * mm});
            skArc(sketch, "E72.4.0.61", {"start": v(292.75, 15.14) * mm, "mid": v(293.14, 14.34) * mm, "end": v(294, 14.17) * mm});
            skArc(sketch, "E72.4.0.62", {"start": v(331, 27.25) * mm, "mid": v(330.3, 26.96) * mm, "end": v(330, 26.25) * mm});
            skArc(sketch, "E72.4.0.63", {"start": v(308.74, -15.27) * mm, "mid": v(309.6, -15.1) * mm, "end": v(310, -14.3) * mm});
            skArc(sketch, "E72.4.0.64", {"start": v(291.57, -10.67) * mm, "mid": v(290.49, -10.89) * mm, "end": v(290, -11.88) * mm});
            skArc(sketch, "E72.4.0.65", {"start": v(331.26, 15.27) * mm, "mid": v(330.4, 15.1) * mm, "end": v(330, 14.3) * mm});
            skArc(sketch, "E72.4.0.66", {"start": v(326.4, -4.8) * mm, "mid": v(326.25, -5.08) * mm, "end": v(326.2, -5.4) * mm});
            skArc(sketch, "E72.4.0.67", {"start": v(326.2, 24.2) * mm, "mid": v(325.9, 24.9) * mm, "end": v(325.2, 25.2) * mm});
            skArc(sketch, "E72.4.0.68", {"start": v(310, 14.3) * mm, "mid": v(309.6, 15.1) * mm, "end": v(308.74, 15.27) * mm});
            skArc(sketch, "E72.4.0.69", {"start": v(346.88, -11.09) * mm, "mid": v(347.15, -10.9) * mm, "end": v(347.25, -10.6) * mm});
            skArc(sketch, "E72.4.0.70", {"start": v(314.8, 25.2) * mm, "mid": v(314.1, 24.9) * mm, "end": v(313.8, 24.2) * mm});
            skArc(sketch, "E72.4.0.71", {"start": v(313.8, -24.2) * mm, "mid": v(314.1, -24.9) * mm, "end": v(314.8, -25.2) * mm});
            skLineSegment(sketch, "E72.5.0.0", {"start": v(372.75, -15.14) * mm, "end": v(372.75, -24) * mm});
            skLineSegment(sketch, "E72.5.0.1", {"start": v(390, -26.25) * mm, "end": v(390, -19.22) * mm});
            skArc(sketch, "E72.5.0.2", {"start": v(376, 27.25) * mm, "mid": v(373.7, 26.3) * mm, "end": v(372.75, 24) * mm});
            skArc(sketch, "E72.5.0.3", {"start": v(427.25, 24) * mm, "mid": v(426.3, 26.3) * mm, "end": v(424, 27.25) * mm});
            skLineSegment(sketch, "E72.5.0.4", {"start": v(372.75, 24) * mm, "end": v(372.75, 15.14) * mm});
            skArc(sketch, "E72.5.0.5", {"start": v(370, -24) * mm, "mid": v(371.76, -28.24) * mm, "end": v(376, -30) * mm});
            skArc(sketch, "E72.5.0.6", {"start": v(424, -27.25) * mm, "mid": v(426.3, -26.3) * mm, "end": v(427.25, -24) * mm});
            skLineSegment(sketch, "E72.5.0.7", {"start": v(393.8, 24.2) * mm, "end": v(393.8, 5.4) * mm});
            skLineSegment(sketch, "E72.5.0.8", {"start": v(374, 14.17) * mm, "end": v(389.26, 18.26) * mm});
            skArc(sketch, "E72.5.0.9", {"start": v(430, 24) * mm, "mid": v(428.24, 28.24) * mm, "end": v(424, 30) * mm});
            skLineSegment(sketch, "E72.5.0.10", {"start": v(370, -11.88) * mm, "end": v(370, -24) * mm});
            skLineSegment(sketch, "E72.5.0.11", {"start": v(406.2, -24.2) * mm, "end": v(406.2, -5.4) * mm});
            skLineSegment(sketch, "E72.5.0.12", {"start": v(430, -24) * mm, "end": v(430, 24) * mm});
            skLineSegment(sketch, "E72.5.0.13", {"start": v(424, 30) * mm, "end": v(376, 30) * mm});
            skLineSegment(sketch, "E72.5.0.14", {"start": v(371.57, 10.67) * mm, "end": v(388.74, 15.27) * mm});
            skLineSegment(sketch, "E72.5.0.15", {"start": v(370, 24) * mm, "end": v(370, 11.88) * mm});
            skLineSegment(sketch, "E72.5.0.16", {"start": v(405.2, 25.2) * mm, "end": v(394.8, 25.2) * mm});
            skLineSegment(sketch, "E72.5.0.17", {"start": v(389.26, -18.26) * mm, "end": v(374, -14.17) * mm});
            skLineSegment(sketch, "E72.5.0.18", {"start": v(411.26, -15.27) * mm, "end": v(426.88, -11.09) * mm});
            skLineSegment(sketch, "E72.5.0.19", {"start": v(427.25, -10.6) * mm, "end": v(427.25, 10.6) * mm});
            skArc(sketch, "E72.5.0.20", {"start": v(372.75, -24) * mm, "mid": v(373.7, -26.3) * mm, "end": v(376, -27.25) * mm});
            skLineSegment(sketch, "E72.5.0.21", {"start": v(376, -27.25) * mm, "end": v(389, -27.25) * mm});
            skLineSegment(sketch, "E72.5.0.22", {"start": v(426.88, 11.09) * mm, "end": v(411.26, 15.27) * mm});
            skLineSegment(sketch, "E72.5.0.23", {"start": v(410, 14.3) * mm, "end": v(410, -14.3) * mm});
            skLineSegment(sketch, "E72.5.0.24", {"start": v(389, 27.25) * mm, "end": v(376, 27.25) * mm});
            skLineSegment(sketch, "E72.5.0.25", {"start": v(424, 27.25) * mm, "end": v(411, 27.25) * mm});
            skLineSegment(sketch, "E72.5.0.26", {"start": v(410, 26.25) * mm, "end": v(410, 19.22) * mm});
            skArc(sketch, "E72.5.0.27", {"start": v(406.4, -4.8) * mm, "mid": v(408, 0) * mm, "end": v(406.4, 4.8) * mm});
            skLineSegment(sketch, "E72.5.0.28", {"start": v(393.8, -5.4) * mm, "end": v(393.8, -24.2) * mm});
            skLineSegment(sketch, "E72.5.0.29", {"start": v(390, 19.22) * mm, "end": v(390, 26.25) * mm});
            skLineSegment(sketch, "E72.5.0.30", {"start": v(410.74, 18.26) * mm, "end": v(426, 14.17) * mm});
            skLineSegment(sketch, "E72.5.0.31", {"start": v(427.25, 15.14) * mm, "end": v(427.25, 24) * mm});
            skArc(sketch, "E72.5.0.32", {"start": v(424, -30) * mm, "mid": v(428.24, -28.24) * mm, "end": v(430, -24) * mm});
            skLineSegment(sketch, "E72.5.0.33", {"start": v(394.8, -25.2) * mm, "end": v(405.2, -25.2) * mm});
            skLineSegment(sketch, "E72.5.0.34", {"start": v(388.74, -15.27) * mm, "end": v(371.57, -10.67) * mm});
            skLineSegment(sketch, "E72.5.0.35", {"start": v(426, -14.17) * mm, "end": v(410.74, -18.26) * mm});
            skLineSegment(sketch, "E72.5.0.36", {"start": v(410, -19.22) * mm, "end": v(410, -26.25) * mm});
            skArc(sketch, "E72.5.0.37", {"start": v(376, 30) * mm, "mid": v(371.76, 28.24) * mm, "end": v(370, 24) * mm});
            skLineSegment(sketch, "E72.5.0.38", {"start": v(406.2, 5.4) * mm, "end": v(406.2, 24.2) * mm});
            skLineSegment(sketch, "E72.5.0.39", {"start": v(376, -30) * mm, "end": v(424, -30) * mm});
            skLineSegment(sketch, "E72.5.0.40", {"start": v(411, -27.25) * mm, "end": v(424, -27.25) * mm});
            skArc(sketch, "E72.5.0.41", {"start": v(393.6, 4.8) * mm, "mid": v(392, 0) * mm, "end": v(393.6, -4.8) * mm});
            skLineSegment(sketch, "E72.5.0.42", {"start": v(427.25, -24) * mm, "end": v(427.25, -15.14) * mm});
            skLineSegment(sketch, "E72.5.0.43", {"start": v(390, 14.3) * mm, "end": v(390, -14.3) * mm});
            skArc(sketch, "E72.5.0.44", {"start": v(389, -27.25) * mm, "mid": v(389.7, -26.96) * mm, "end": v(390, -26.25) * mm});
            skArc(sketch, "E72.5.0.45", {"start": v(410.74, -18.26) * mm, "mid": v(410.2, -18.61) * mm, "end": v(410, -19.22) * mm});
            skArc(sketch, "E72.5.0.46", {"start": v(406.2, 5.4) * mm, "mid": v(406.25, 5.08) * mm, "end": v(406.4, 4.8) * mm});
            skArc(sketch, "E72.5.0.47", {"start": v(389.26, 18.26) * mm, "mid": v(389.8, 18.61) * mm, "end": v(390, 19.22) * mm});
            skArc(sketch, "E72.5.0.48", {"start": v(410, 19.22) * mm, "mid": v(410.2, 18.61) * mm, "end": v(410.74, 18.26) * mm});
            skArc(sketch, "E72.5.0.49", {"start": v(427.25, 10.6) * mm, "mid": v(427.15, 10.9) * mm, "end": v(426.88, 11.09) * mm});
            skArc(sketch, "E72.5.0.50", {"start": v(374, -14.17) * mm, "mid": v(373.14, -14.34) * mm, "end": v(372.75, -15.14) * mm});
            skArc(sketch, "E72.5.0.51", {"start": v(405.2, -25.2) * mm, "mid": v(405.9, -24.9) * mm, "end": v(406.2, -24.2) * mm});
            skArc(sketch, "E72.5.0.52", {"start": v(410, -14.3) * mm, "mid": v(410.4, -15.1) * mm, "end": v(411.26, -15.27) * mm});
            skArc(sketch, "E72.5.0.53", {"start": v(393.8, -5.4) * mm, "mid": v(393.75, -5.08) * mm, "end": v(393.6, -4.8) * mm});
            skArc(sketch, "E72.5.0.54", {"start": v(370, 11.88) * mm, "mid": v(370.49, 10.89) * mm, "end": v(371.57, 10.67) * mm});
            skArc(sketch, "E72.5.0.55", {"start": v(393.6, 4.8) * mm, "mid": v(393.75, 5.08) * mm, "end": v(393.8, 5.4) * mm});
            skArc(sketch, "E72.5.0.56", {"start": v(390, -19.22) * mm, "mid": v(389.8, -18.61) * mm, "end": v(389.26, -18.26) * mm});
            skArc(sketch, "E72.5.0.57", {"start": v(410, -26.25) * mm, "mid": v(410.3, -26.96) * mm, "end": v(411, -27.25) * mm});
            skArc(sketch, "E72.5.0.58", {"start": v(427.25, -15.14) * mm, "mid": v(426.86, -14.34) * mm, "end": v(426, -14.17) * mm});
            skArc(sketch, "E72.5.0.59", {"start": v(390, 26.25) * mm, "mid": v(389.7, 26.96) * mm, "end": v(389, 27.25) * mm});
            skArc(sketch, "E72.5.0.60", {"start": v(426, 14.17) * mm, "mid": v(426.86, 14.34) * mm, "end": v(427.25, 15.14) * mm});
            skArc(sketch, "E72.5.0.61", {"start": v(372.75, 15.14) * mm, "mid": v(373.14, 14.34) * mm, "end": v(374, 14.17) * mm});
            skArc(sketch, "E72.5.0.62", {"start": v(411, 27.25) * mm, "mid": v(410.3, 26.96) * mm, "end": v(410, 26.25) * mm});
            skArc(sketch, "E72.5.0.63", {"start": v(388.74, -15.27) * mm, "mid": v(389.6, -15.1) * mm, "end": v(390, -14.3) * mm});
            skArc(sketch, "E72.5.0.64", {"start": v(371.57, -10.67) * mm, "mid": v(370.49, -10.89) * mm, "end": v(370, -11.88) * mm});
            skArc(sketch, "E72.5.0.65", {"start": v(411.26, 15.27) * mm, "mid": v(410.4, 15.1) * mm, "end": v(410, 14.3) * mm});
            skArc(sketch, "E72.5.0.66", {"start": v(406.4, -4.8) * mm, "mid": v(406.25, -5.08) * mm, "end": v(406.2, -5.4) * mm});
            skArc(sketch, "E72.5.0.67", {"start": v(406.2, 24.2) * mm, "mid": v(405.9, 24.9) * mm, "end": v(405.2, 25.2) * mm});
            skArc(sketch, "E72.5.0.68", {"start": v(390, 14.3) * mm, "mid": v(389.6, 15.1) * mm, "end": v(388.74, 15.27) * mm});
            skArc(sketch, "E72.5.0.69", {"start": v(426.88, -11.09) * mm, "mid": v(427.15, -10.9) * mm, "end": v(427.25, -10.6) * mm});
            skArc(sketch, "E72.5.0.70", {"start": v(394.8, 25.2) * mm, "mid": v(394.1, 24.9) * mm, "end": v(393.8, 24.2) * mm});
            skArc(sketch, "E72.5.0.71", {"start": v(393.8, -24.2) * mm, "mid": v(394.1, -24.9) * mm, "end": v(394.8, -25.2) * mm});
            skLineSegment(sketch, "E72.6.0.0", {"start": v(452.75, -15.14) * mm, "end": v(452.75, -24) * mm});
            skLineSegment(sketch, "E72.6.0.1", {"start": v(470, -26.25) * mm, "end": v(470, -19.22) * mm});
            skArc(sketch, "E72.6.0.2", {"start": v(456, 27.25) * mm, "mid": v(453.7, 26.3) * mm, "end": v(452.75, 24) * mm});
            skArc(sketch, "E72.6.0.3", {"start": v(507.25, 24) * mm, "mid": v(506.3, 26.3) * mm, "end": v(504, 27.25) * mm});
            skLineSegment(sketch, "E72.6.0.4", {"start": v(452.75, 24) * mm, "end": v(452.75, 15.14) * mm});
            skArc(sketch, "E72.6.0.5", {"start": v(450, -24) * mm, "mid": v(451.76, -28.24) * mm, "end": v(456, -30) * mm});
            skArc(sketch, "E72.6.0.6", {"start": v(504, -27.25) * mm, "mid": v(506.3, -26.3) * mm, "end": v(507.25, -24) * mm});
            skLineSegment(sketch, "E72.6.0.7", {"start": v(473.8, 24.2) * mm, "end": v(473.8, 5.4) * mm});
            skLineSegment(sketch, "E72.6.0.8", {"start": v(454, 14.17) * mm, "end": v(469.26, 18.26) * mm});
            skArc(sketch, "E72.6.0.9", {"start": v(510, 24) * mm, "mid": v(508.24, 28.24) * mm, "end": v(504, 30) * mm});
            skLineSegment(sketch, "E72.6.0.10", {"start": v(450, -11.88) * mm, "end": v(450, -24) * mm});
            skLineSegment(sketch, "E72.6.0.11", {"start": v(486.2, -24.2) * mm, "end": v(486.2, -5.4) * mm});
            skLineSegment(sketch, "E72.6.0.12", {"start": v(510, -24) * mm, "end": v(510, 24) * mm});
            skLineSegment(sketch, "E72.6.0.13", {"start": v(504, 30) * mm, "end": v(456, 30) * mm});
            skLineSegment(sketch, "E72.6.0.14", {"start": v(451.57, 10.67) * mm, "end": v(468.74, 15.27) * mm});
            skLineSegment(sketch, "E72.6.0.15", {"start": v(450, 24) * mm, "end": v(450, 11.88) * mm});
            skLineSegment(sketch, "E72.6.0.16", {"start": v(485.2, 25.2) * mm, "end": v(474.8, 25.2) * mm});
            skLineSegment(sketch, "E72.6.0.17", {"start": v(469.26, -18.26) * mm, "end": v(454, -14.17) * mm});
            skLineSegment(sketch, "E72.6.0.18", {"start": v(491.26, -15.27) * mm, "end": v(506.88, -11.09) * mm});
            skLineSegment(sketch, "E72.6.0.19", {"start": v(507.25, -10.6) * mm, "end": v(507.25, 10.6) * mm});
            skArc(sketch, "E72.6.0.20", {"start": v(452.75, -24) * mm, "mid": v(453.7, -26.3) * mm, "end": v(456, -27.25) * mm});
            skLineSegment(sketch, "E72.6.0.21", {"start": v(456, -27.25) * mm, "end": v(469, -27.25) * mm});
            skLineSegment(sketch, "E72.6.0.22", {"start": v(506.88, 11.09) * mm, "end": v(491.26, 15.27) * mm});
            skLineSegment(sketch, "E72.6.0.23", {"start": v(490, 14.3) * mm, "end": v(490, -14.3) * mm});
            skLineSegment(sketch, "E72.6.0.24", {"start": v(469, 27.25) * mm, "end": v(456, 27.25) * mm});
            skLineSegment(sketch, "E72.6.0.25", {"start": v(504, 27.25) * mm, "end": v(491, 27.25) * mm});
            skLineSegment(sketch, "E72.6.0.26", {"start": v(490, 26.25) * mm, "end": v(490, 19.22) * mm});
            skArc(sketch, "E72.6.0.27", {"start": v(486.4, -4.8) * mm, "mid": v(488, 0) * mm, "end": v(486.4, 4.8) * mm});
            skLineSegment(sketch, "E72.6.0.28", {"start": v(473.8, -5.4) * mm, "end": v(473.8, -24.2) * mm});
            skLineSegment(sketch, "E72.6.0.29", {"start": v(470, 19.22) * mm, "end": v(470, 26.25) * mm});
            skLineSegment(sketch, "E72.6.0.30", {"start": v(490.74, 18.26) * mm, "end": v(506, 14.17) * mm});
            skLineSegment(sketch, "E72.6.0.31", {"start": v(507.25, 15.14) * mm, "end": v(507.25, 24) * mm});
            skArc(sketch, "E72.6.0.32", {"start": v(504, -30) * mm, "mid": v(508.24, -28.24) * mm, "end": v(510, -24) * mm});
            skLineSegment(sketch, "E72.6.0.33", {"start": v(474.8, -25.2) * mm, "end": v(485.2, -25.2) * mm});
            skLineSegment(sketch, "E72.6.0.34", {"start": v(468.74, -15.27) * mm, "end": v(451.57, -10.67) * mm});
            skLineSegment(sketch, "E72.6.0.35", {"start": v(506, -14.17) * mm, "end": v(490.74, -18.26) * mm});
            skLineSegment(sketch, "E72.6.0.36", {"start": v(490, -19.22) * mm, "end": v(490, -26.25) * mm});
            skArc(sketch, "E72.6.0.37", {"start": v(456, 30) * mm, "mid": v(451.76, 28.24) * mm, "end": v(450, 24) * mm});
            skLineSegment(sketch, "E72.6.0.38", {"start": v(486.2, 5.4) * mm, "end": v(486.2, 24.2) * mm});
            skLineSegment(sketch, "E72.6.0.39", {"start": v(456, -30) * mm, "end": v(504, -30) * mm});
            skLineSegment(sketch, "E72.6.0.40", {"start": v(491, -27.25) * mm, "end": v(504, -27.25) * mm});
            skArc(sketch, "E72.6.0.41", {"start": v(473.6, 4.8) * mm, "mid": v(472, 0) * mm, "end": v(473.6, -4.8) * mm});
            skLineSegment(sketch, "E72.6.0.42", {"start": v(507.25, -24) * mm, "end": v(507.25, -15.14) * mm});
            skLineSegment(sketch, "E72.6.0.43", {"start": v(470, 14.3) * mm, "end": v(470, -14.3) * mm});
            skArc(sketch, "E72.6.0.44", {"start": v(469, -27.25) * mm, "mid": v(469.7, -26.96) * mm, "end": v(470, -26.25) * mm});
            skArc(sketch, "E72.6.0.45", {"start": v(490.74, -18.26) * mm, "mid": v(490.2, -18.61) * mm, "end": v(490, -19.22) * mm});
            skArc(sketch, "E72.6.0.46", {"start": v(486.2, 5.4) * mm, "mid": v(486.25, 5.08) * mm, "end": v(486.4, 4.8) * mm});
            skArc(sketch, "E72.6.0.47", {"start": v(469.26, 18.26) * mm, "mid": v(469.8, 18.61) * mm, "end": v(470, 19.22) * mm});
            skArc(sketch, "E72.6.0.48", {"start": v(490, 19.22) * mm, "mid": v(490.2, 18.61) * mm, "end": v(490.74, 18.26) * mm});
            skArc(sketch, "E72.6.0.49", {"start": v(507.25, 10.6) * mm, "mid": v(507.15, 10.9) * mm, "end": v(506.88, 11.09) * mm});
            skArc(sketch, "E72.6.0.50", {"start": v(454, -14.17) * mm, "mid": v(453.14, -14.34) * mm, "end": v(452.75, -15.14) * mm});
            skArc(sketch, "E72.6.0.51", {"start": v(485.2, -25.2) * mm, "mid": v(485.9, -24.9) * mm, "end": v(486.2, -24.2) * mm});
            skArc(sketch, "E72.6.0.52", {"start": v(490, -14.3) * mm, "mid": v(490.4, -15.1) * mm, "end": v(491.26, -15.27) * mm});
            skArc(sketch, "E72.6.0.53", {"start": v(473.8, -5.4) * mm, "mid": v(473.75, -5.08) * mm, "end": v(473.6, -4.8) * mm});
            skArc(sketch, "E72.6.0.54", {"start": v(450, 11.88) * mm, "mid": v(450.49, 10.89) * mm, "end": v(451.57, 10.67) * mm});
            skArc(sketch, "E72.6.0.55", {"start": v(473.6, 4.8) * mm, "mid": v(473.75, 5.08) * mm, "end": v(473.8, 5.4) * mm});
            skArc(sketch, "E72.6.0.56", {"start": v(470, -19.22) * mm, "mid": v(469.8, -18.61) * mm, "end": v(469.26, -18.26) * mm});
            skArc(sketch, "E72.6.0.57", {"start": v(490, -26.25) * mm, "mid": v(490.3, -26.96) * mm, "end": v(491, -27.25) * mm});
            skArc(sketch, "E72.6.0.58", {"start": v(507.25, -15.14) * mm, "mid": v(506.86, -14.34) * mm, "end": v(506, -14.17) * mm});
            skArc(sketch, "E72.6.0.59", {"start": v(470, 26.25) * mm, "mid": v(469.7, 26.96) * mm, "end": v(469, 27.25) * mm});
            skArc(sketch, "E72.6.0.60", {"start": v(506, 14.17) * mm, "mid": v(506.86, 14.34) * mm, "end": v(507.25, 15.14) * mm});
            skArc(sketch, "E72.6.0.61", {"start": v(452.75, 15.14) * mm, "mid": v(453.14, 14.34) * mm, "end": v(454, 14.17) * mm});
            skArc(sketch, "E72.6.0.62", {"start": v(491, 27.25) * mm, "mid": v(490.3, 26.96) * mm, "end": v(490, 26.25) * mm});
            skArc(sketch, "E72.6.0.63", {"start": v(468.74, -15.27) * mm, "mid": v(469.6, -15.1) * mm, "end": v(470, -14.3) * mm});
            skArc(sketch, "E72.6.0.64", {"start": v(451.57, -10.67) * mm, "mid": v(450.49, -10.89) * mm, "end": v(450, -11.88) * mm});
            skArc(sketch, "E72.6.0.65", {"start": v(491.26, 15.27) * mm, "mid": v(490.4, 15.1) * mm, "end": v(490, 14.3) * mm});
            skArc(sketch, "E72.6.0.66", {"start": v(486.4, -4.8) * mm, "mid": v(486.25, -5.08) * mm, "end": v(486.2, -5.4) * mm});
            skArc(sketch, "E72.6.0.67", {"start": v(486.2, 24.2) * mm, "mid": v(485.9, 24.9) * mm, "end": v(485.2, 25.2) * mm});
            skArc(sketch, "E72.6.0.68", {"start": v(470, 14.3) * mm, "mid": v(469.6, 15.1) * mm, "end": v(468.74, 15.27) * mm});
            skArc(sketch, "E72.6.0.69", {"start": v(506.88, -11.09) * mm, "mid": v(507.15, -10.9) * mm, "end": v(507.25, -10.6) * mm});
            skArc(sketch, "E72.6.0.70", {"start": v(474.8, 25.2) * mm, "mid": v(474.1, 24.9) * mm, "end": v(473.8, 24.2) * mm});
            skArc(sketch, "E72.6.0.71", {"start": v(473.8, -24.2) * mm, "mid": v(474.1, -24.9) * mm, "end": v(474.8, -25.2) * mm});
            skLineSegment(sketch, "E72.7.0.0", {"start": v(532.75, -15.14) * mm, "end": v(532.75, -24) * mm});
            skLineSegment(sketch, "E72.7.0.1", {"start": v(550, -26.25) * mm, "end": v(550, -19.22) * mm});
            skArc(sketch, "E72.7.0.2", {"start": v(536, 27.25) * mm, "mid": v(533.7, 26.3) * mm, "end": v(532.75, 24) * mm});
            skArc(sketch, "E72.7.0.3", {"start": v(587.25, 24) * mm, "mid": v(586.3, 26.3) * mm, "end": v(584, 27.25) * mm});
            skLineSegment(sketch, "E72.7.0.4", {"start": v(532.75, 24) * mm, "end": v(532.75, 15.14) * mm});
            skArc(sketch, "E72.7.0.5", {"start": v(530, -24) * mm, "mid": v(531.76, -28.24) * mm, "end": v(536, -30) * mm});
            skArc(sketch, "E72.7.0.6", {"start": v(584, -27.25) * mm, "mid": v(586.3, -26.3) * mm, "end": v(587.25, -24) * mm});
            skLineSegment(sketch, "E72.7.0.7", {"start": v(553.8, 24.2) * mm, "end": v(553.8, 5.4) * mm});
            skLineSegment(sketch, "E72.7.0.8", {"start": v(534, 14.17) * mm, "end": v(549.26, 18.26) * mm});
            skArc(sketch, "E72.7.0.9", {"start": v(590, 24) * mm, "mid": v(588.24, 28.24) * mm, "end": v(584, 30) * mm});
            skLineSegment(sketch, "E72.7.0.10", {"start": v(530, -11.88) * mm, "end": v(530, -24) * mm});
            skLineSegment(sketch, "E72.7.0.11", {"start": v(566.2, -24.2) * mm, "end": v(566.2, -5.4) * mm});
            skLineSegment(sketch, "E72.7.0.12", {"start": v(590, -24) * mm, "end": v(590, 24) * mm});
            skLineSegment(sketch, "E72.7.0.13", {"start": v(584, 30) * mm, "end": v(536, 30) * mm});
            skLineSegment(sketch, "E72.7.0.14", {"start": v(531.57, 10.67) * mm, "end": v(548.74, 15.27) * mm});
            skLineSegment(sketch, "E72.7.0.15", {"start": v(530, 24) * mm, "end": v(530, 11.88) * mm});
            skLineSegment(sketch, "E72.7.0.16", {"start": v(565.2, 25.2) * mm, "end": v(554.8, 25.2) * mm});
            skLineSegment(sketch, "E72.7.0.17", {"start": v(549.26, -18.26) * mm, "end": v(534, -14.17) * mm});
            skLineSegment(sketch, "E72.7.0.18", {"start": v(571.26, -15.27) * mm, "end": v(586.88, -11.09) * mm});
            skLineSegment(sketch, "E72.7.0.19", {"start": v(587.25, -10.6) * mm, "end": v(587.25, 10.6) * mm});
            skArc(sketch, "E72.7.0.20", {"start": v(532.75, -24) * mm, "mid": v(533.7, -26.3) * mm, "end": v(536, -27.25) * mm});
            skLineSegment(sketch, "E72.7.0.21", {"start": v(536, -27.25) * mm, "end": v(549, -27.25) * mm});
            skLineSegment(sketch, "E72.7.0.22", {"start": v(586.88, 11.09) * mm, "end": v(571.26, 15.27) * mm});
            skLineSegment(sketch, "E72.7.0.23", {"start": v(570, 14.3) * mm, "end": v(570, -14.3) * mm});
            skLineSegment(sketch, "E72.7.0.24", {"start": v(549, 27.25) * mm, "end": v(536, 27.25) * mm});
            skLineSegment(sketch, "E72.7.0.25", {"start": v(584, 27.25) * mm, "end": v(571, 27.25) * mm});
            skLineSegment(sketch, "E72.7.0.26", {"start": v(570, 26.25) * mm, "end": v(570, 19.22) * mm});
            skArc(sketch, "E72.7.0.27", {"start": v(566.4, -4.8) * mm, "mid": v(568, 0) * mm, "end": v(566.4, 4.8) * mm});
            skLineSegment(sketch, "E72.7.0.28", {"start": v(553.8, -5.4) * mm, "end": v(553.8, -24.2) * mm});
            skLineSegment(sketch, "E72.7.0.29", {"start": v(550, 19.22) * mm, "end": v(550, 26.25) * mm});
            skLineSegment(sketch, "E72.7.0.30", {"start": v(570.74, 18.26) * mm, "end": v(586, 14.17) * mm});
            skLineSegment(sketch, "E72.7.0.31", {"start": v(587.25, 15.14) * mm, "end": v(587.25, 24) * mm});
            skArc(sketch, "E72.7.0.32", {"start": v(584, -30) * mm, "mid": v(588.24, -28.24) * mm, "end": v(590, -24) * mm});
            skLineSegment(sketch, "E72.7.0.33", {"start": v(554.8, -25.2) * mm, "end": v(565.2, -25.2) * mm});
            skLineSegment(sketch, "E72.7.0.34", {"start": v(548.74, -15.27) * mm, "end": v(531.57, -10.67) * mm});
            skLineSegment(sketch, "E72.7.0.35", {"start": v(586, -14.17) * mm, "end": v(570.74, -18.26) * mm});
            skLineSegment(sketch, "E72.7.0.36", {"start": v(570, -19.22) * mm, "end": v(570, -26.25) * mm});
            skArc(sketch, "E72.7.0.37", {"start": v(536, 30) * mm, "mid": v(531.76, 28.24) * mm, "end": v(530, 24) * mm});
            skLineSegment(sketch, "E72.7.0.38", {"start": v(566.2, 5.4) * mm, "end": v(566.2, 24.2) * mm});
            skLineSegment(sketch, "E72.7.0.39", {"start": v(536, -30) * mm, "end": v(584, -30) * mm});
            skLineSegment(sketch, "E72.7.0.40", {"start": v(571, -27.25) * mm, "end": v(584, -27.25) * mm});
            skArc(sketch, "E72.7.0.41", {"start": v(553.6, 4.8) * mm, "mid": v(552, 0) * mm, "end": v(553.6, -4.8) * mm});
            skLineSegment(sketch, "E72.7.0.42", {"start": v(587.25, -24) * mm, "end": v(587.25, -15.14) * mm});
            skLineSegment(sketch, "E72.7.0.43", {"start": v(550, 14.3) * mm, "end": v(550, -14.3) * mm});
            skArc(sketch, "E72.7.0.44", {"start": v(549, -27.25) * mm, "mid": v(549.7, -26.96) * mm, "end": v(550, -26.25) * mm});
            skArc(sketch, "E72.7.0.45", {"start": v(570.74, -18.26) * mm, "mid": v(570.2, -18.61) * mm, "end": v(570, -19.22) * mm});
            skArc(sketch, "E72.7.0.46", {"start": v(566.2, 5.4) * mm, "mid": v(566.25, 5.08) * mm, "end": v(566.4, 4.8) * mm});
            skArc(sketch, "E72.7.0.47", {"start": v(549.26, 18.26) * mm, "mid": v(549.8, 18.61) * mm, "end": v(550, 19.22) * mm});
            skArc(sketch, "E72.7.0.48", {"start": v(570, 19.22) * mm, "mid": v(570.2, 18.61) * mm, "end": v(570.74, 18.26) * mm});
            skArc(sketch, "E72.7.0.49", {"start": v(587.25, 10.6) * mm, "mid": v(587.15, 10.9) * mm, "end": v(586.88, 11.09) * mm});
            skArc(sketch, "E72.7.0.50", {"start": v(534, -14.17) * mm, "mid": v(533.14, -14.34) * mm, "end": v(532.75, -15.14) * mm});
            skArc(sketch, "E72.7.0.51", {"start": v(565.2, -25.2) * mm, "mid": v(565.9, -24.9) * mm, "end": v(566.2, -24.2) * mm});
            skArc(sketch, "E72.7.0.52", {"start": v(570, -14.3) * mm, "mid": v(570.4, -15.1) * mm, "end": v(571.26, -15.27) * mm});
            skArc(sketch, "E72.7.0.53", {"start": v(553.8, -5.4) * mm, "mid": v(553.75, -5.08) * mm, "end": v(553.6, -4.8) * mm});
            skArc(sketch, "E72.7.0.54", {"start": v(530, 11.88) * mm, "mid": v(530.49, 10.89) * mm, "end": v(531.57, 10.67) * mm});
            skArc(sketch, "E72.7.0.55", {"start": v(553.6, 4.8) * mm, "mid": v(553.75, 5.08) * mm, "end": v(553.8, 5.4) * mm});
            skArc(sketch, "E72.7.0.56", {"start": v(550, -19.22) * mm, "mid": v(549.8, -18.61) * mm, "end": v(549.26, -18.26) * mm});
            skArc(sketch, "E72.7.0.57", {"start": v(570, -26.25) * mm, "mid": v(570.3, -26.96) * mm, "end": v(571, -27.25) * mm});
            skArc(sketch, "E72.7.0.58", {"start": v(587.25, -15.14) * mm, "mid": v(586.86, -14.34) * mm, "end": v(586, -14.17) * mm});
            skArc(sketch, "E72.7.0.59", {"start": v(550, 26.25) * mm, "mid": v(549.7, 26.96) * mm, "end": v(549, 27.25) * mm});
            skArc(sketch, "E72.7.0.60", {"start": v(586, 14.17) * mm, "mid": v(586.86, 14.34) * mm, "end": v(587.25, 15.14) * mm});
            skArc(sketch, "E72.7.0.61", {"start": v(532.75, 15.14) * mm, "mid": v(533.14, 14.34) * mm, "end": v(534, 14.17) * mm});
            skArc(sketch, "E72.7.0.62", {"start": v(571, 27.25) * mm, "mid": v(570.3, 26.96) * mm, "end": v(570, 26.25) * mm});
            skArc(sketch, "E72.7.0.63", {"start": v(548.74, -15.27) * mm, "mid": v(549.6, -15.1) * mm, "end": v(550, -14.3) * mm});
            skArc(sketch, "E72.7.0.64", {"start": v(531.57, -10.67) * mm, "mid": v(530.49, -10.89) * mm, "end": v(530, -11.88) * mm});
            skArc(sketch, "E72.7.0.65", {"start": v(571.26, 15.27) * mm, "mid": v(570.4, 15.1) * mm, "end": v(570, 14.3) * mm});
            skArc(sketch, "E72.7.0.66", {"start": v(566.4, -4.8) * mm, "mid": v(566.25, -5.08) * mm, "end": v(566.2, -5.4) * mm});
            skArc(sketch, "E72.7.0.67", {"start": v(566.2, 24.2) * mm, "mid": v(565.9, 24.9) * mm, "end": v(565.2, 25.2) * mm});
            skArc(sketch, "E72.7.0.68", {"start": v(550, 14.3) * mm, "mid": v(549.6, 15.1) * mm, "end": v(548.74, 15.27) * mm});
            skArc(sketch, "E72.7.0.69", {"start": v(586.88, -11.09) * mm, "mid": v(587.15, -10.9) * mm, "end": v(587.25, -10.6) * mm});
            skArc(sketch, "E72.7.0.70", {"start": v(554.8, 25.2) * mm, "mid": v(554.1, 24.9) * mm, "end": v(553.8, 24.2) * mm});
            skArc(sketch, "E72.7.0.71", {"start": v(553.8, -24.2) * mm, "mid": v(554.1, -24.9) * mm, "end": v(554.8, -25.2) * mm});
            skLineSegment(sketch, "E72.8.0.0", {"start": v(612.75, -15.14) * mm, "end": v(612.75, -24) * mm});
            skLineSegment(sketch, "E72.8.0.1", {"start": v(630, -26.25) * mm, "end": v(630, -19.22) * mm});
            skArc(sketch, "E72.8.0.2", {"start": v(616, 27.25) * mm, "mid": v(613.7, 26.3) * mm, "end": v(612.75, 24) * mm});
            skArc(sketch, "E72.8.0.3", {"start": v(667.25, 24) * mm, "mid": v(666.3, 26.3) * mm, "end": v(664, 27.25) * mm});
            skLineSegment(sketch, "E72.8.0.4", {"start": v(612.75, 24) * mm, "end": v(612.75, 15.14) * mm});
            skArc(sketch, "E72.8.0.5", {"start": v(610, -24) * mm, "mid": v(611.76, -28.24) * mm, "end": v(616, -30) * mm});
            skArc(sketch, "E72.8.0.6", {"start": v(664, -27.25) * mm, "mid": v(666.3, -26.3) * mm, "end": v(667.25, -24) * mm});
            skLineSegment(sketch, "E72.8.0.7", {"start": v(633.8, 24.2) * mm, "end": v(633.8, 5.4) * mm});
            skLineSegment(sketch, "E72.8.0.8", {"start": v(614, 14.17) * mm, "end": v(629.26, 18.26) * mm});
            skArc(sketch, "E72.8.0.9", {"start": v(670, 24) * mm, "mid": v(668.24, 28.24) * mm, "end": v(664, 30) * mm});
            skLineSegment(sketch, "E72.8.0.10", {"start": v(610, -11.88) * mm, "end": v(610, -24) * mm});
            skLineSegment(sketch, "E72.8.0.11", {"start": v(646.2, -24.2) * mm, "end": v(646.2, -5.4) * mm});
            skLineSegment(sketch, "E72.8.0.12", {"start": v(670, -24) * mm, "end": v(670, 24) * mm});
            skLineSegment(sketch, "E72.8.0.13", {"start": v(664, 30) * mm, "end": v(616, 30) * mm});
            skLineSegment(sketch, "E72.8.0.14", {"start": v(611.57, 10.67) * mm, "end": v(628.74, 15.27) * mm});
            skLineSegment(sketch, "E72.8.0.15", {"start": v(610, 24) * mm, "end": v(610, 11.88) * mm});
            skLineSegment(sketch, "E72.8.0.16", {"start": v(645.2, 25.2) * mm, "end": v(634.8, 25.2) * mm});
            skLineSegment(sketch, "E72.8.0.17", {"start": v(629.26, -18.26) * mm, "end": v(614, -14.17) * mm});
            skLineSegment(sketch, "E72.8.0.18", {"start": v(651.26, -15.27) * mm, "end": v(666.88, -11.09) * mm});
            skLineSegment(sketch, "E72.8.0.19", {"start": v(667.25, -10.6) * mm, "end": v(667.25, 10.6) * mm});
            skArc(sketch, "E72.8.0.20", {"start": v(612.75, -24) * mm, "mid": v(613.7, -26.3) * mm, "end": v(616, -27.25) * mm});
            skLineSegment(sketch, "E72.8.0.21", {"start": v(616, -27.25) * mm, "end": v(629, -27.25) * mm});
            skLineSegment(sketch, "E72.8.0.22", {"start": v(666.88, 11.09) * mm, "end": v(651.26, 15.27) * mm});
            skLineSegment(sketch, "E72.8.0.23", {"start": v(650, 14.3) * mm, "end": v(650, -14.3) * mm});
            skLineSegment(sketch, "E72.8.0.24", {"start": v(629, 27.25) * mm, "end": v(616, 27.25) * mm});
            skLineSegment(sketch, "E72.8.0.25", {"start": v(664, 27.25) * mm, "end": v(651, 27.25) * mm});
            skLineSegment(sketch, "E72.8.0.26", {"start": v(650, 26.25) * mm, "end": v(650, 19.22) * mm});
            skArc(sketch, "E72.8.0.27", {"start": v(646.4, -4.8) * mm, "mid": v(648, 0) * mm, "end": v(646.4, 4.8) * mm});
            skLineSegment(sketch, "E72.8.0.28", {"start": v(633.8, -5.4) * mm, "end": v(633.8, -24.2) * mm});
            skLineSegment(sketch, "E72.8.0.29", {"start": v(630, 19.22) * mm, "end": v(630, 26.25) * mm});
            skLineSegment(sketch, "E72.8.0.30", {"start": v(650.74, 18.26) * mm, "end": v(666, 14.17) * mm});
            skLineSegment(sketch, "E72.8.0.31", {"start": v(667.25, 15.14) * mm, "end": v(667.25, 24) * mm});
            skArc(sketch, "E72.8.0.32", {"start": v(664, -30) * mm, "mid": v(668.24, -28.24) * mm, "end": v(670, -24) * mm});
            skLineSegment(sketch, "E72.8.0.33", {"start": v(634.8, -25.2) * mm, "end": v(645.2, -25.2) * mm});
            skLineSegment(sketch, "E72.8.0.34", {"start": v(628.74, -15.27) * mm, "end": v(611.57, -10.67) * mm});
            skLineSegment(sketch, "E72.8.0.35", {"start": v(666, -14.17) * mm, "end": v(650.74, -18.26) * mm});
            skLineSegment(sketch, "E72.8.0.36", {"start": v(650, -19.22) * mm, "end": v(650, -26.25) * mm});
            skArc(sketch, "E72.8.0.37", {"start": v(616, 30) * mm, "mid": v(611.76, 28.24) * mm, "end": v(610, 24) * mm});
            skLineSegment(sketch, "E72.8.0.38", {"start": v(646.2, 5.4) * mm, "end": v(646.2, 24.2) * mm});
            skLineSegment(sketch, "E72.8.0.39", {"start": v(616, -30) * mm, "end": v(664, -30) * mm});
            skLineSegment(sketch, "E72.8.0.40", {"start": v(651, -27.25) * mm, "end": v(664, -27.25) * mm});
            skArc(sketch, "E72.8.0.41", {"start": v(633.6, 4.8) * mm, "mid": v(632, 0) * mm, "end": v(633.6, -4.8) * mm});
            skLineSegment(sketch, "E72.8.0.42", {"start": v(667.25, -24) * mm, "end": v(667.25, -15.14) * mm});
            skLineSegment(sketch, "E72.8.0.43", {"start": v(630, 14.3) * mm, "end": v(630, -14.3) * mm});
            skArc(sketch, "E72.8.0.44", {"start": v(629, -27.25) * mm, "mid": v(629.7, -26.96) * mm, "end": v(630, -26.25) * mm});
            skArc(sketch, "E72.8.0.45", {"start": v(650.74, -18.26) * mm, "mid": v(650.2, -18.61) * mm, "end": v(650, -19.22) * mm});
            skArc(sketch, "E72.8.0.46", {"start": v(646.2, 5.4) * mm, "mid": v(646.25, 5.08) * mm, "end": v(646.4, 4.8) * mm});
            skArc(sketch, "E72.8.0.47", {"start": v(629.26, 18.26) * mm, "mid": v(629.8, 18.61) * mm, "end": v(630, 19.22) * mm});
            skArc(sketch, "E72.8.0.48", {"start": v(650, 19.22) * mm, "mid": v(650.2, 18.61) * mm, "end": v(650.74, 18.26) * mm});
            skArc(sketch, "E72.8.0.49", {"start": v(667.25, 10.6) * mm, "mid": v(667.15, 10.9) * mm, "end": v(666.88, 11.09) * mm});
            skArc(sketch, "E72.8.0.50", {"start": v(614, -14.17) * mm, "mid": v(613.14, -14.34) * mm, "end": v(612.75, -15.14) * mm});
            skArc(sketch, "E72.8.0.51", {"start": v(645.2, -25.2) * mm, "mid": v(645.9, -24.9) * mm, "end": v(646.2, -24.2) * mm});
            skArc(sketch, "E72.8.0.52", {"start": v(650, -14.3) * mm, "mid": v(650.4, -15.1) * mm, "end": v(651.26, -15.27) * mm});
            skArc(sketch, "E72.8.0.53", {"start": v(633.8, -5.4) * mm, "mid": v(633.75, -5.08) * mm, "end": v(633.6, -4.8) * mm});
            skArc(sketch, "E72.8.0.54", {"start": v(610, 11.88) * mm, "mid": v(610.49, 10.89) * mm, "end": v(611.57, 10.67) * mm});
            skArc(sketch, "E72.8.0.55", {"start": v(633.6, 4.8) * mm, "mid": v(633.75, 5.08) * mm, "end": v(633.8, 5.4) * mm});
            skArc(sketch, "E72.8.0.56", {"start": v(630, -19.22) * mm, "mid": v(629.8, -18.61) * mm, "end": v(629.26, -18.26) * mm});
            skArc(sketch, "E72.8.0.57", {"start": v(650, -26.25) * mm, "mid": v(650.3, -26.96) * mm, "end": v(651, -27.25) * mm});
            skArc(sketch, "E72.8.0.58", {"start": v(667.25, -15.14) * mm, "mid": v(666.86, -14.34) * mm, "end": v(666, -14.17) * mm});
            skArc(sketch, "E72.8.0.59", {"start": v(630, 26.25) * mm, "mid": v(629.7, 26.96) * mm, "end": v(629, 27.25) * mm});
            skArc(sketch, "E72.8.0.60", {"start": v(666, 14.17) * mm, "mid": v(666.86, 14.34) * mm, "end": v(667.25, 15.14) * mm});
            skArc(sketch, "E72.8.0.61", {"start": v(612.75, 15.14) * mm, "mid": v(613.14, 14.34) * mm, "end": v(614, 14.17) * mm});
            skArc(sketch, "E72.8.0.62", {"start": v(651, 27.25) * mm, "mid": v(650.3, 26.96) * mm, "end": v(650, 26.25) * mm});
            skArc(sketch, "E72.8.0.63", {"start": v(628.74, -15.27) * mm, "mid": v(629.6, -15.1) * mm, "end": v(630, -14.3) * mm});
            skArc(sketch, "E72.8.0.64", {"start": v(611.57, -10.67) * mm, "mid": v(610.49, -10.89) * mm, "end": v(610, -11.88) * mm});
            skArc(sketch, "E72.8.0.65", {"start": v(651.26, 15.27) * mm, "mid": v(650.4, 15.1) * mm, "end": v(650, 14.3) * mm});
            skArc(sketch, "E72.8.0.66", {"start": v(646.4, -4.8) * mm, "mid": v(646.25, -5.08) * mm, "end": v(646.2, -5.4) * mm});
            skArc(sketch, "E72.8.0.67", {"start": v(646.2, 24.2) * mm, "mid": v(645.9, 24.9) * mm, "end": v(645.2, 25.2) * mm});
            skArc(sketch, "E72.8.0.68", {"start": v(630, 14.3) * mm, "mid": v(629.6, 15.1) * mm, "end": v(628.74, 15.27) * mm});
            skArc(sketch, "E72.8.0.69", {"start": v(666.88, -11.09) * mm, "mid": v(667.15, -10.9) * mm, "end": v(667.25, -10.6) * mm});
            skArc(sketch, "E72.8.0.70", {"start": v(634.8, 25.2) * mm, "mid": v(634.1, 24.9) * mm, "end": v(633.8, 24.2) * mm});
            skArc(sketch, "E72.8.0.71", {"start": v(633.8, -24.2) * mm, "mid": v(634.1, -24.9) * mm, "end": v(634.8, -25.2) * mm});
            skLineSegment(sketch, "E72.9.0.0", {"start": v(692.75, -15.14) * mm, "end": v(692.75, -24) * mm});
            skLineSegment(sketch, "E72.9.0.1", {"start": v(710, -26.25) * mm, "end": v(710, -19.22) * mm});
            skArc(sketch, "E72.9.0.2", {"start": v(696, 27.25) * mm, "mid": v(693.7, 26.3) * mm, "end": v(692.75, 24) * mm});
            skArc(sketch, "E72.9.0.3", {"start": v(747.25, 24) * mm, "mid": v(746.3, 26.3) * mm, "end": v(744, 27.25) * mm});
            skLineSegment(sketch, "E72.9.0.4", {"start": v(692.75, 24) * mm, "end": v(692.75, 15.14) * mm});
            skArc(sketch, "E72.9.0.5", {"start": v(690, -24) * mm, "mid": v(691.76, -28.24) * mm, "end": v(696, -30) * mm});
            skArc(sketch, "E72.9.0.6", {"start": v(744, -27.25) * mm, "mid": v(746.3, -26.3) * mm, "end": v(747.25, -24) * mm});
            skLineSegment(sketch, "E72.9.0.7", {"start": v(713.8, 24.2) * mm, "end": v(713.8, 5.4) * mm});
            skLineSegment(sketch, "E72.9.0.8", {"start": v(694, 14.17) * mm, "end": v(709.26, 18.26) * mm});
            skArc(sketch, "E72.9.0.9", {"start": v(750, 24) * mm, "mid": v(748.24, 28.24) * mm, "end": v(744, 30) * mm});
            skLineSegment(sketch, "E72.9.0.10", {"start": v(690, -11.88) * mm, "end": v(690, -24) * mm});
            skLineSegment(sketch, "E72.9.0.11", {"start": v(726.2, -24.2) * mm, "end": v(726.2, -5.4) * mm});
            skLineSegment(sketch, "E72.9.0.12", {"start": v(750, -24) * mm, "end": v(750, 24) * mm});
            skLineSegment(sketch, "E72.9.0.13", {"start": v(744, 30) * mm, "end": v(696, 30) * mm});
            skLineSegment(sketch, "E72.9.0.14", {"start": v(691.57, 10.67) * mm, "end": v(708.74, 15.27) * mm});
            skLineSegment(sketch, "E72.9.0.15", {"start": v(690, 24) * mm, "end": v(690, 11.88) * mm});
            skLineSegment(sketch, "E72.9.0.16", {"start": v(725.2, 25.2) * mm, "end": v(714.8, 25.2) * mm});
            skLineSegment(sketch, "E72.9.0.17", {"start": v(709.26, -18.26) * mm, "end": v(694, -14.17) * mm});
            skLineSegment(sketch, "E72.9.0.18", {"start": v(731.26, -15.27) * mm, "end": v(746.88, -11.09) * mm});
            skLineSegment(sketch, "E72.9.0.19", {"start": v(747.25, -10.6) * mm, "end": v(747.25, 10.6) * mm});
            skArc(sketch, "E72.9.0.20", {"start": v(692.75, -24) * mm, "mid": v(693.7, -26.3) * mm, "end": v(696, -27.25) * mm});
            skLineSegment(sketch, "E72.9.0.21", {"start": v(696, -27.25) * mm, "end": v(709, -27.25) * mm});
            skLineSegment(sketch, "E72.9.0.22", {"start": v(746.88, 11.09) * mm, "end": v(731.26, 15.27) * mm});
            skLineSegment(sketch, "E72.9.0.23", {"start": v(730, 14.3) * mm, "end": v(730, -14.3) * mm});
            skLineSegment(sketch, "E72.9.0.24", {"start": v(709, 27.25) * mm, "end": v(696, 27.25) * mm});
            skLineSegment(sketch, "E72.9.0.25", {"start": v(744, 27.25) * mm, "end": v(731, 27.25) * mm});
            skLineSegment(sketch, "E72.9.0.26", {"start": v(730, 26.25) * mm, "end": v(730, 19.22) * mm});
            skArc(sketch, "E72.9.0.27", {"start": v(726.4, -4.8) * mm, "mid": v(728, 0) * mm, "end": v(726.4, 4.8) * mm});
            skLineSegment(sketch, "E72.9.0.28", {"start": v(713.8, -5.4) * mm, "end": v(713.8, -24.2) * mm});
            skLineSegment(sketch, "E72.9.0.29", {"start": v(710, 19.22) * mm, "end": v(710, 26.25) * mm});
            skLineSegment(sketch, "E72.9.0.30", {"start": v(730.74, 18.26) * mm, "end": v(746, 14.17) * mm});
            skLineSegment(sketch, "E72.9.0.31", {"start": v(747.25, 15.14) * mm, "end": v(747.25, 24) * mm});
            skArc(sketch, "E72.9.0.32", {"start": v(744, -30) * mm, "mid": v(748.24, -28.24) * mm, "end": v(750, -24) * mm});
            skLineSegment(sketch, "E72.9.0.33", {"start": v(714.8, -25.2) * mm, "end": v(725.2, -25.2) * mm});
            skLineSegment(sketch, "E72.9.0.34", {"start": v(708.74, -15.27) * mm, "end": v(691.57, -10.67) * mm});
            skLineSegment(sketch, "E72.9.0.35", {"start": v(746, -14.17) * mm, "end": v(730.74, -18.26) * mm});
            skLineSegment(sketch, "E72.9.0.36", {"start": v(730, -19.22) * mm, "end": v(730, -26.25) * mm});
            skArc(sketch, "E72.9.0.37", {"start": v(696, 30) * mm, "mid": v(691.76, 28.24) * mm, "end": v(690, 24) * mm});
            skLineSegment(sketch, "E72.9.0.38", {"start": v(726.2, 5.4) * mm, "end": v(726.2, 24.2) * mm});
            skLineSegment(sketch, "E72.9.0.39", {"start": v(696, -30) * mm, "end": v(744, -30) * mm});
            skLineSegment(sketch, "E72.9.0.40", {"start": v(731, -27.25) * mm, "end": v(744, -27.25) * mm});
            skArc(sketch, "E72.9.0.41", {"start": v(713.6, 4.8) * mm, "mid": v(712, 0) * mm, "end": v(713.6, -4.8) * mm});
            skLineSegment(sketch, "E72.9.0.42", {"start": v(747.25, -24) * mm, "end": v(747.25, -15.14) * mm});
            skLineSegment(sketch, "E72.9.0.43", {"start": v(710, 14.3) * mm, "end": v(710, -14.3) * mm});
            skArc(sketch, "E72.9.0.44", {"start": v(709, -27.25) * mm, "mid": v(709.7, -26.96) * mm, "end": v(710, -26.25) * mm});
            skArc(sketch, "E72.9.0.45", {"start": v(730.74, -18.26) * mm, "mid": v(730.2, -18.61) * mm, "end": v(730, -19.22) * mm});
            skArc(sketch, "E72.9.0.46", {"start": v(726.2, 5.4) * mm, "mid": v(726.25, 5.08) * mm, "end": v(726.4, 4.8) * mm});
            skArc(sketch, "E72.9.0.47", {"start": v(709.26, 18.26) * mm, "mid": v(709.8, 18.61) * mm, "end": v(710, 19.22) * mm});
            skArc(sketch, "E72.9.0.48", {"start": v(730, 19.22) * mm, "mid": v(730.2, 18.61) * mm, "end": v(730.74, 18.26) * mm});
            skArc(sketch, "E72.9.0.49", {"start": v(747.25, 10.6) * mm, "mid": v(747.15, 10.9) * mm, "end": v(746.88, 11.09) * mm});
            skArc(sketch, "E72.9.0.50", {"start": v(694, -14.17) * mm, "mid": v(693.14, -14.34) * mm, "end": v(692.75, -15.14) * mm});
            skArc(sketch, "E72.9.0.51", {"start": v(725.2, -25.2) * mm, "mid": v(725.9, -24.9) * mm, "end": v(726.2, -24.2) * mm});
            skArc(sketch, "E72.9.0.52", {"start": v(730, -14.3) * mm, "mid": v(730.4, -15.1) * mm, "end": v(731.26, -15.27) * mm});
            skArc(sketch, "E72.9.0.53", {"start": v(713.8, -5.4) * mm, "mid": v(713.75, -5.08) * mm, "end": v(713.6, -4.8) * mm});
            skArc(sketch, "E72.9.0.54", {"start": v(690, 11.88) * mm, "mid": v(690.49, 10.89) * mm, "end": v(691.57, 10.67) * mm});
            skArc(sketch, "E72.9.0.55", {"start": v(713.6, 4.8) * mm, "mid": v(713.75, 5.08) * mm, "end": v(713.8, 5.4) * mm});
            skArc(sketch, "E72.9.0.56", {"start": v(710, -19.22) * mm, "mid": v(709.8, -18.61) * mm, "end": v(709.26, -18.26) * mm});
            skArc(sketch, "E72.9.0.57", {"start": v(730, -26.25) * mm, "mid": v(730.3, -26.96) * mm, "end": v(731, -27.25) * mm});
            skArc(sketch, "E72.9.0.58", {"start": v(747.25, -15.14) * mm, "mid": v(746.86, -14.34) * mm, "end": v(746, -14.17) * mm});
            skArc(sketch, "E72.9.0.59", {"start": v(710, 26.25) * mm, "mid": v(709.7, 26.96) * mm, "end": v(709, 27.25) * mm});
            skArc(sketch, "E72.9.0.60", {"start": v(746, 14.17) * mm, "mid": v(746.86, 14.34) * mm, "end": v(747.25, 15.14) * mm});
            skArc(sketch, "E72.9.0.61", {"start": v(692.75, 15.14) * mm, "mid": v(693.14, 14.34) * mm, "end": v(694, 14.17) * mm});
            skArc(sketch, "E72.9.0.62", {"start": v(731, 27.25) * mm, "mid": v(730.3, 26.96) * mm, "end": v(730, 26.25) * mm});
            skArc(sketch, "E72.9.0.63", {"start": v(708.74, -15.27) * mm, "mid": v(709.6, -15.1) * mm, "end": v(710, -14.3) * mm});
            skArc(sketch, "E72.9.0.64", {"start": v(691.57, -10.67) * mm, "mid": v(690.49, -10.89) * mm, "end": v(690, -11.88) * mm});
            skArc(sketch, "E72.9.0.65", {"start": v(731.26, 15.27) * mm, "mid": v(730.4, 15.1) * mm, "end": v(730, 14.3) * mm});
            skArc(sketch, "E72.9.0.66", {"start": v(726.4, -4.8) * mm, "mid": v(726.25, -5.08) * mm, "end": v(726.2, -5.4) * mm});
            skArc(sketch, "E72.9.0.67", {"start": v(726.2, 24.2) * mm, "mid": v(725.9, 24.9) * mm, "end": v(725.2, 25.2) * mm});
            skArc(sketch, "E72.9.0.68", {"start": v(710, 14.3) * mm, "mid": v(709.6, 15.1) * mm, "end": v(708.74, 15.27) * mm});
            skArc(sketch, "E72.9.0.69", {"start": v(746.88, -11.09) * mm, "mid": v(747.15, -10.9) * mm, "end": v(747.25, -10.6) * mm});
            skArc(sketch, "E72.9.0.70", {"start": v(714.8, 25.2) * mm, "mid": v(714.1, 24.9) * mm, "end": v(713.8, 24.2) * mm});
            skArc(sketch, "E72.9.0.71", {"start": v(713.8, -24.2) * mm, "mid": v(714.1, -24.9) * mm, "end": v(714.8, -25.2) * mm});
            skLineSegment(sketch, "E72.direction1", {"start": v(-24, -30) * mm, "end": v(56, -30) * mm, "construction": true});
            skSolve(sketch);
        }
        {
            var Q0;
            Q0=makeQuery(id+"F0.imprint","IMPRINT",FACE,{"disambiguationData":[TD([[makeQuery(id+"F0.imprint","IMPRINT",EDGE,{"derivedFrom":sQuery(id+"F0.wireOp",EDGE,"E0")}),-1.0]])]});
            extrude(context, id + "F1", {"entities" : qUnion([Q0]), "depth" : 1600 * mm, "offsetDistance" : 25 * mm});
        }
        {
            var Q0;
            Q0=makeQuery(id+"F0.imprint","IMPRINT",FACE,{"disambiguationData":[TD([[makeQuery(id+"F0.imprint","IMPRINT",EDGE,{"derivedFrom":sQuery(id+"F0.wireOp",EDGE,"E72.1.0.0")}),-1.0]])]});
            extrude(context, id + "F2", {"entities" : qUnion([Q0]), "depth" : 1000 * mm, "offsetDistance" : 25 * mm});
        }
    });
